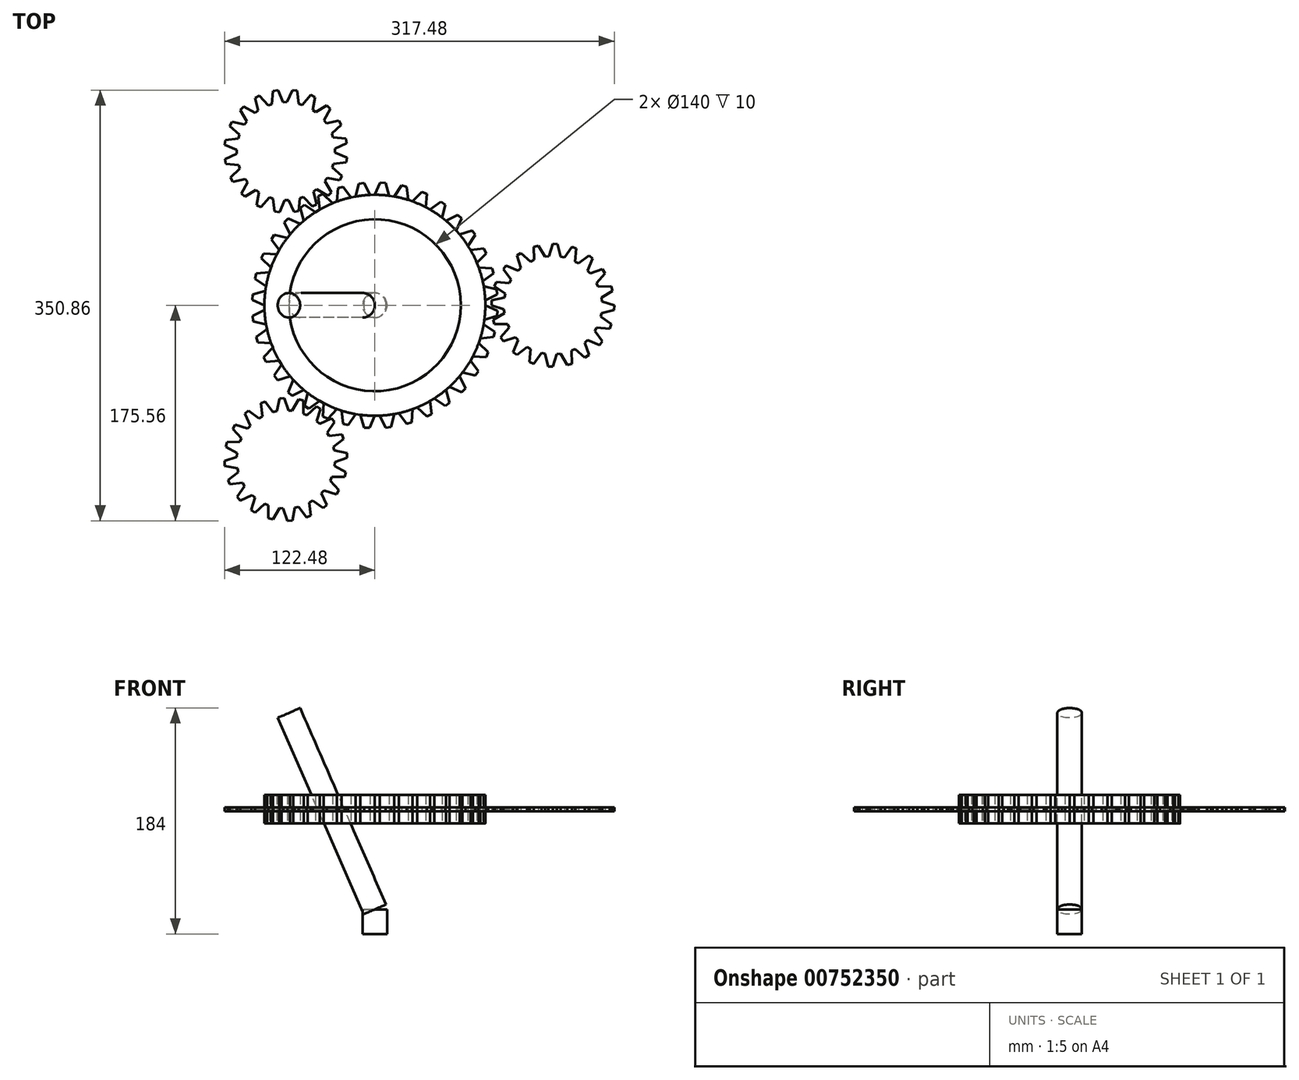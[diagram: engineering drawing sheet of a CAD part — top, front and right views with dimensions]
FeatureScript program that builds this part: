
annotation { "Feature Type Name" : "Feature", "Feature Type Description" : "" }
export const myFeature = defineFeature(function(context is Context, id is Id, definition is map)
    precondition{}
    {
        {
            var Q0;
            Q0=qCreatedBy(makeId("Top.planeOp"),FACE);
            var sketch = newSketch(context, id + "F0", { "sketchPlane" : qUnion([Q0])});
            skLineSegment(sketch, "E0", {"start": v(90, 0) * mm, "end": v(100, 0) * mm});
            skLineSegment(sketch, "E1.4.0", {"start": v(88.63, -15.63) * mm, "end": v(98.48, -17.36) * mm});
            skPoint(sketch, "E1.center", {"position": v(0, 0) * mm});
            skLineSegment(sketch, "E2", {"start": v(90, 0) * mm, "end": v(99.9, -4.36) * mm});
            skLineSegment(sketch, "E3", {"start": v(99.9, -4.36) * mm, "end": v(99.62, -8.72) * mm});
            skLineSegment(sketch, "E4", {"start": v(99.62, -8.72) * mm, "end": v(89.23, -11.75) * mm});
            skLineSegment(sketch, "E5", {"start": v(89.23, -11.75) * mm, "end": v(88.63, -15.63) * mm});
            skLineSegment(sketch, "E6.1.0", {"start": v(88.63, 15.63) * mm, "end": v(99.14, 13.05) * mm});
            skLineSegment(sketch, "E6.1.1", {"start": v(99.14, 13.05) * mm, "end": v(99.62, 8.72) * mm});
            skLineSegment(sketch, "E6.1.2", {"start": v(99.62, 8.72) * mm, "end": v(89.91, 3.93) * mm});
            skLineSegment(sketch, "E6.1.3", {"start": v(89.91, 3.93) * mm, "end": v(90, 0) * mm});
            skLineSegment(sketch, "E6.2.0", {"start": v(84.57, 30.78) * mm, "end": v(95.37, 30.07) * mm});
            skLineSegment(sketch, "E6.2.1", {"start": v(95.37, 30.07) * mm, "end": v(96.6, 25.88) * mm});
            skLineSegment(sketch, "E6.2.2", {"start": v(96.6, 25.88) * mm, "end": v(87.87, 19.48) * mm});
            skLineSegment(sketch, "E6.2.3", {"start": v(87.87, 19.48) * mm, "end": v(88.63, 15.63) * mm});
            skLineSegment(sketch, "E6.3.0", {"start": v(77.94, 45) * mm, "end": v(88.7, 46.17) * mm});
            skLineSegment(sketch, "E6.3.1", {"start": v(88.7, 46.17) * mm, "end": v(90.63, 42.26) * mm});
            skLineSegment(sketch, "E6.3.2", {"start": v(90.63, 42.26) * mm, "end": v(83.15, 34.44) * mm});
            skLineSegment(sketch, "E6.3.3", {"start": v(83.15, 34.44) * mm, "end": v(84.57, 30.78) * mm});
            skLineSegment(sketch, "E6.4.0", {"start": v(68.94, 57.85) * mm, "end": v(79.34, 60.88) * mm});
            skLineSegment(sketch, "E6.4.1", {"start": v(79.34, 60.88) * mm, "end": v(81.92, 57.36) * mm});
            skLineSegment(sketch, "E6.4.2", {"start": v(81.92, 57.36) * mm, "end": v(75.9, 48.36) * mm});
            skLineSegment(sketch, "E6.4.3", {"start": v(75.9, 48.36) * mm, "end": v(77.94, 45) * mm});
            skLineSegment(sketch, "E6.5.0", {"start": v(57.85, 68.94) * mm, "end": v(67.56, 73.73) * mm});
            skLineSegment(sketch, "E6.5.1", {"start": v(67.56, 73.73) * mm, "end": v(70.71, 70.71) * mm});
            skLineSegment(sketch, "E6.5.2", {"start": v(70.71, 70.71) * mm, "end": v(66.35, 60.8) * mm});
            skLineSegment(sketch, "E6.5.3", {"start": v(66.35, 60.8) * mm, "end": v(68.94, 57.85) * mm});
            skLineSegment(sketch, "E6.6.0", {"start": v(45, 77.94) * mm, "end": v(53.73, 84.34) * mm});
            skLineSegment(sketch, "E6.6.1", {"start": v(53.73, 84.34) * mm, "end": v(57.36, 81.92) * mm});
            skLineSegment(sketch, "E6.6.2", {"start": v(57.36, 81.92) * mm, "end": v(54.79, 71.4) * mm});
            skLineSegment(sketch, "E6.6.3", {"start": v(54.79, 71.4) * mm, "end": v(57.85, 68.94) * mm});
            skLineSegment(sketch, "E6.7.0", {"start": v(30.78, 84.57) * mm, "end": v(38.27, 92.39) * mm});
            skLineSegment(sketch, "E6.7.1", {"start": v(38.27, 92.39) * mm, "end": v(42.26, 90.63) * mm});
            skLineSegment(sketch, "E6.7.2", {"start": v(42.26, 90.63) * mm, "end": v(41.56, 79.83) * mm});
            skLineSegment(sketch, "E6.7.3", {"start": v(41.56, 79.83) * mm, "end": v(45, 77.94) * mm});
            skLineSegment(sketch, "E6.8.0", {"start": v(15.63, 88.63) * mm, "end": v(21.64, 97.63) * mm});
            skLineSegment(sketch, "E6.8.1", {"start": v(21.64, 97.63) * mm, "end": v(25.88, 96.6) * mm});
            skLineSegment(sketch, "E6.8.2", {"start": v(25.88, 96.6) * mm, "end": v(27.06, 85.83) * mm});
            skLineSegment(sketch, "E6.8.3", {"start": v(27.06, 85.83) * mm, "end": v(30.78, 84.57) * mm});
            skLineSegment(sketch, "E6.9.0", {"start": v(0, 90) * mm, "end": v(4.36, 99.9) * mm});
            skLineSegment(sketch, "E6.9.1", {"start": v(4.36, 99.9) * mm, "end": v(8.72, 99.62) * mm});
            skLineSegment(sketch, "E6.9.2", {"start": v(8.72, 99.62) * mm, "end": v(11.75, 89.23) * mm});
            skLineSegment(sketch, "E6.9.3", {"start": v(11.75, 89.23) * mm, "end": v(15.63, 88.63) * mm});
            skLineSegment(sketch, "E6.10.0", {"start": v(-15.63, 88.63) * mm, "end": v(-13.05, 99.14) * mm});
            skLineSegment(sketch, "E6.10.1", {"start": v(-13.05, 99.14) * mm, "end": v(-8.72, 99.62) * mm});
            skLineSegment(sketch, "E6.10.2", {"start": v(-8.72, 99.62) * mm, "end": v(-3.93, 89.91) * mm});
            skLineSegment(sketch, "E6.10.3", {"start": v(-3.93, 89.91) * mm, "end": v(0, 90) * mm});
            skLineSegment(sketch, "E6.11.0", {"start": v(-30.78, 84.57) * mm, "end": v(-30.07, 95.37) * mm});
            skLineSegment(sketch, "E6.11.1", {"start": v(-30.07, 95.37) * mm, "end": v(-25.88, 96.6) * mm});
            skLineSegment(sketch, "E6.11.2", {"start": v(-25.88, 96.6) * mm, "end": v(-19.48, 87.87) * mm});
            skLineSegment(sketch, "E6.11.3", {"start": v(-19.48, 87.87) * mm, "end": v(-15.63, 88.63) * mm});
            skLineSegment(sketch, "E6.12.0", {"start": v(-45, 77.94) * mm, "end": v(-46.17, 88.7) * mm});
            skLineSegment(sketch, "E6.12.1", {"start": v(-46.17, 88.7) * mm, "end": v(-42.26, 90.63) * mm});
            skLineSegment(sketch, "E6.12.2", {"start": v(-42.26, 90.63) * mm, "end": v(-34.44, 83.15) * mm});
            skLineSegment(sketch, "E6.12.3", {"start": v(-34.44, 83.15) * mm, "end": v(-30.78, 84.57) * mm});
            skLineSegment(sketch, "E6.13.0", {"start": v(-57.85, 68.94) * mm, "end": v(-60.88, 79.34) * mm});
            skLineSegment(sketch, "E6.13.1", {"start": v(-60.88, 79.34) * mm, "end": v(-57.36, 81.92) * mm});
            skLineSegment(sketch, "E6.13.2", {"start": v(-57.36, 81.92) * mm, "end": v(-48.36, 75.9) * mm});
            skLineSegment(sketch, "E6.13.3", {"start": v(-48.36, 75.9) * mm, "end": v(-45, 77.94) * mm});
            skLineSegment(sketch, "E6.14.0", {"start": v(-68.94, 57.85) * mm, "end": v(-73.73, 67.56) * mm});
            skLineSegment(sketch, "E6.14.1", {"start": v(-73.73, 67.56) * mm, "end": v(-70.71, 70.71) * mm});
            skLineSegment(sketch, "E6.14.2", {"start": v(-70.71, 70.71) * mm, "end": v(-60.8, 66.35) * mm});
            skLineSegment(sketch, "E6.14.3", {"start": v(-60.8, 66.35) * mm, "end": v(-57.85, 68.94) * mm});
            skLineSegment(sketch, "E6.15.0", {"start": v(-77.94, 45) * mm, "end": v(-84.34, 53.73) * mm});
            skLineSegment(sketch, "E6.15.1", {"start": v(-84.34, 53.73) * mm, "end": v(-81.92, 57.36) * mm});
            skLineSegment(sketch, "E6.15.2", {"start": v(-81.92, 57.36) * mm, "end": v(-71.4, 54.79) * mm});
            skLineSegment(sketch, "E6.15.3", {"start": v(-71.4, 54.79) * mm, "end": v(-68.94, 57.85) * mm});
            skLineSegment(sketch, "E6.16.0", {"start": v(-84.57, 30.78) * mm, "end": v(-92.39, 38.27) * mm});
            skLineSegment(sketch, "E6.16.1", {"start": v(-92.39, 38.27) * mm, "end": v(-90.63, 42.26) * mm});
            skLineSegment(sketch, "E6.16.2", {"start": v(-90.63, 42.26) * mm, "end": v(-79.83, 41.56) * mm});
            skLineSegment(sketch, "E6.16.3", {"start": v(-79.83, 41.56) * mm, "end": v(-77.94, 45) * mm});
            skLineSegment(sketch, "E6.17.0", {"start": v(-88.63, 15.63) * mm, "end": v(-97.63, 21.64) * mm});
            skLineSegment(sketch, "E6.17.1", {"start": v(-97.63, 21.64) * mm, "end": v(-96.6, 25.88) * mm});
            skLineSegment(sketch, "E6.17.2", {"start": v(-96.6, 25.88) * mm, "end": v(-85.83, 27.06) * mm});
            skLineSegment(sketch, "E6.17.3", {"start": v(-85.83, 27.06) * mm, "end": v(-84.57, 30.78) * mm});
            skLineSegment(sketch, "E6.18.0", {"start": v(-90, 0) * mm, "end": v(-99.9, 4.36) * mm});
            skLineSegment(sketch, "E6.18.1", {"start": v(-99.9, 4.36) * mm, "end": v(-99.62, 8.72) * mm});
            skLineSegment(sketch, "E6.18.2", {"start": v(-99.62, 8.72) * mm, "end": v(-89.23, 11.75) * mm});
            skLineSegment(sketch, "E6.18.3", {"start": v(-89.23, 11.75) * mm, "end": v(-88.63, 15.63) * mm});
            skLineSegment(sketch, "E6.19.0", {"start": v(-88.63, -15.63) * mm, "end": v(-99.14, -13.05) * mm});
            skLineSegment(sketch, "E6.19.1", {"start": v(-99.14, -13.05) * mm, "end": v(-99.62, -8.72) * mm});
            skLineSegment(sketch, "E6.19.2", {"start": v(-99.62, -8.72) * mm, "end": v(-89.91, -3.93) * mm});
            skLineSegment(sketch, "E6.19.3", {"start": v(-89.91, -3.93) * mm, "end": v(-90, 0) * mm});
            skLineSegment(sketch, "E6.20.0", {"start": v(-84.57, -30.78) * mm, "end": v(-95.37, -30.07) * mm});
            skLineSegment(sketch, "E6.20.1", {"start": v(-95.37, -30.07) * mm, "end": v(-96.6, -25.88) * mm});
            skLineSegment(sketch, "E6.20.2", {"start": v(-96.6, -25.88) * mm, "end": v(-87.87, -19.48) * mm});
            skLineSegment(sketch, "E6.20.3", {"start": v(-87.87, -19.48) * mm, "end": v(-88.63, -15.63) * mm});
            skLineSegment(sketch, "E6.21.0", {"start": v(-77.94, -45) * mm, "end": v(-88.7, -46.17) * mm});
            skLineSegment(sketch, "E6.21.1", {"start": v(-88.7, -46.17) * mm, "end": v(-90.63, -42.26) * mm});
            skLineSegment(sketch, "E6.21.2", {"start": v(-90.63, -42.26) * mm, "end": v(-83.15, -34.44) * mm});
            skLineSegment(sketch, "E6.21.3", {"start": v(-83.15, -34.44) * mm, "end": v(-84.57, -30.78) * mm});
            skLineSegment(sketch, "E6.22.0", {"start": v(-68.94, -57.85) * mm, "end": v(-79.34, -60.88) * mm});
            skLineSegment(sketch, "E6.22.1", {"start": v(-79.34, -60.88) * mm, "end": v(-81.92, -57.36) * mm});
            skLineSegment(sketch, "E6.22.2", {"start": v(-81.92, -57.36) * mm, "end": v(-75.9, -48.36) * mm});
            skLineSegment(sketch, "E6.22.3", {"start": v(-75.9, -48.36) * mm, "end": v(-77.94, -45) * mm});
            skLineSegment(sketch, "E6.23.0", {"start": v(-57.85, -68.94) * mm, "end": v(-67.56, -73.73) * mm});
            skLineSegment(sketch, "E6.23.1", {"start": v(-67.56, -73.73) * mm, "end": v(-70.71, -70.71) * mm});
            skLineSegment(sketch, "E6.23.2", {"start": v(-70.71, -70.71) * mm, "end": v(-66.35, -60.8) * mm});
            skLineSegment(sketch, "E6.23.3", {"start": v(-66.35, -60.8) * mm, "end": v(-68.94, -57.85) * mm});
            skLineSegment(sketch, "E6.24.0", {"start": v(-45, -77.94) * mm, "end": v(-53.73, -84.34) * mm});
            skLineSegment(sketch, "E6.24.1", {"start": v(-53.73, -84.34) * mm, "end": v(-57.36, -81.92) * mm});
            skLineSegment(sketch, "E6.24.2", {"start": v(-57.36, -81.92) * mm, "end": v(-54.79, -71.4) * mm});
            skLineSegment(sketch, "E6.24.3", {"start": v(-54.79, -71.4) * mm, "end": v(-57.85, -68.94) * mm});
            skLineSegment(sketch, "E6.25.0", {"start": v(-30.78, -84.57) * mm, "end": v(-38.27, -92.39) * mm});
            skLineSegment(sketch, "E6.25.1", {"start": v(-38.27, -92.39) * mm, "end": v(-42.26, -90.63) * mm});
            skLineSegment(sketch, "E6.25.2", {"start": v(-42.26, -90.63) * mm, "end": v(-41.56, -79.83) * mm});
            skLineSegment(sketch, "E6.25.3", {"start": v(-41.56, -79.83) * mm, "end": v(-45, -77.94) * mm});
            skLineSegment(sketch, "E6.26.0", {"start": v(-15.63, -88.63) * mm, "end": v(-21.64, -97.63) * mm});
            skLineSegment(sketch, "E6.26.1", {"start": v(-21.64, -97.63) * mm, "end": v(-25.88, -96.6) * mm});
            skLineSegment(sketch, "E6.26.2", {"start": v(-25.88, -96.6) * mm, "end": v(-27.06, -85.83) * mm});
            skLineSegment(sketch, "E6.26.3", {"start": v(-27.06, -85.83) * mm, "end": v(-30.78, -84.57) * mm});
            skLineSegment(sketch, "E6.27.0", {"start": v(0, -90) * mm, "end": v(-4.36, -99.9) * mm});
            skLineSegment(sketch, "E6.27.1", {"start": v(-4.36, -99.9) * mm, "end": v(-8.72, -99.62) * mm});
            skLineSegment(sketch, "E6.27.2", {"start": v(-8.72, -99.62) * mm, "end": v(-11.75, -89.23) * mm});
            skLineSegment(sketch, "E6.27.3", {"start": v(-11.75, -89.23) * mm, "end": v(-15.63, -88.63) * mm});
            skLineSegment(sketch, "E6.28.0", {"start": v(15.63, -88.63) * mm, "end": v(13.05, -99.14) * mm});
            skLineSegment(sketch, "E6.28.1", {"start": v(13.05, -99.14) * mm, "end": v(8.72, -99.62) * mm});
            skLineSegment(sketch, "E6.28.2", {"start": v(8.72, -99.62) * mm, "end": v(3.93, -89.91) * mm});
            skLineSegment(sketch, "E6.28.3", {"start": v(3.93, -89.91) * mm, "end": v(0, -90) * mm});
            skLineSegment(sketch, "E6.29.0", {"start": v(30.78, -84.57) * mm, "end": v(30.07, -95.37) * mm});
            skLineSegment(sketch, "E6.29.1", {"start": v(30.07, -95.37) * mm, "end": v(25.88, -96.6) * mm});
            skLineSegment(sketch, "E6.29.2", {"start": v(25.88, -96.6) * mm, "end": v(19.48, -87.87) * mm});
            skLineSegment(sketch, "E6.29.3", {"start": v(19.48, -87.87) * mm, "end": v(15.63, -88.63) * mm});
            skLineSegment(sketch, "E6.30.0", {"start": v(45, -77.94) * mm, "end": v(46.17, -88.7) * mm});
            skLineSegment(sketch, "E6.30.1", {"start": v(46.17, -88.7) * mm, "end": v(42.26, -90.63) * mm});
            skLineSegment(sketch, "E6.30.2", {"start": v(42.26, -90.63) * mm, "end": v(34.44, -83.15) * mm});
            skLineSegment(sketch, "E6.30.3", {"start": v(34.44, -83.15) * mm, "end": v(30.78, -84.57) * mm});
            skLineSegment(sketch, "E6.31.0", {"start": v(57.85, -68.94) * mm, "end": v(60.88, -79.34) * mm});
            skLineSegment(sketch, "E6.31.1", {"start": v(60.88, -79.34) * mm, "end": v(57.36, -81.92) * mm});
            skLineSegment(sketch, "E6.31.2", {"start": v(57.36, -81.92) * mm, "end": v(48.36, -75.9) * mm});
            skLineSegment(sketch, "E6.31.3", {"start": v(48.36, -75.9) * mm, "end": v(45, -77.94) * mm});
            skLineSegment(sketch, "E6.32.0", {"start": v(68.94, -57.85) * mm, "end": v(73.73, -67.56) * mm});
            skLineSegment(sketch, "E6.32.1", {"start": v(73.73, -67.56) * mm, "end": v(70.71, -70.71) * mm});
            skLineSegment(sketch, "E6.32.2", {"start": v(70.71, -70.71) * mm, "end": v(60.8, -66.35) * mm});
            skLineSegment(sketch, "E6.32.3", {"start": v(60.8, -66.35) * mm, "end": v(57.85, -68.94) * mm});
            skLineSegment(sketch, "E6.33.0", {"start": v(77.94, -45) * mm, "end": v(84.34, -53.73) * mm});
            skLineSegment(sketch, "E6.33.1", {"start": v(84.34, -53.73) * mm, "end": v(81.92, -57.36) * mm});
            skLineSegment(sketch, "E6.33.2", {"start": v(81.92, -57.36) * mm, "end": v(71.4, -54.79) * mm});
            skLineSegment(sketch, "E6.33.3", {"start": v(71.4, -54.79) * mm, "end": v(68.94, -57.85) * mm});
            skLineSegment(sketch, "E6.34.0", {"start": v(84.57, -30.78) * mm, "end": v(92.39, -38.27) * mm});
            skLineSegment(sketch, "E6.34.1", {"start": v(92.39, -38.27) * mm, "end": v(90.63, -42.26) * mm});
            skLineSegment(sketch, "E6.34.2", {"start": v(90.63, -42.26) * mm, "end": v(79.83, -41.56) * mm});
            skLineSegment(sketch, "E6.34.3", {"start": v(79.83, -41.56) * mm, "end": v(77.94, -45) * mm});
            skLineSegment(sketch, "E6.35.0", {"start": v(88.63, -15.63) * mm, "end": v(97.63, -21.64) * mm});
            skLineSegment(sketch, "E6.35.1", {"start": v(97.63, -21.64) * mm, "end": v(96.6, -25.88) * mm});
            skLineSegment(sketch, "E6.35.2", {"start": v(96.6, -25.88) * mm, "end": v(85.83, -27.06) * mm});
            skLineSegment(sketch, "E6.35.3", {"start": v(85.83, -27.06) * mm, "end": v(84.57, -30.78) * mm});
            skLineSegment(sketch, "E7", {"start": v(145, 0) * mm, "end": v(90, 0) * mm});
            skPoint(sketch, "E8.center", {"position": v(145, 0) * mm});
            skLineSegment(sketch, "E8.anchor1", {"start": v(145, 0) * mm, "end": v(90, 0) * mm, "construction": true});
            skLineSegment(sketch, "E9", {"start": v(95.15, 3.92) * mm, "end": v(105.5, 6.26) * mm});
            skLineSegment(sketch, "E10", {"start": v(95.15, 3.92) * mm, "end": v(95, 0) * mm});
            skLineSegment(sketch, "E11", {"start": v(105.5, 6.26) * mm, "end": v(106.1, 9.34) * mm});
            skLineSegment(sketch, "E12", {"start": v(106.1, 9.34) * mm, "end": v(97.45, 15.45) * mm});
            skLineSegment(sketch, "E13.1.0", {"start": v(96.38, -11.67) * mm, "end": v(97.45, -15.45) * mm});
            skLineSegment(sketch, "E13.1.1", {"start": v(96.38, -11.67) * mm, "end": v(105.5, -6.26) * mm});
            skLineSegment(sketch, "E13.1.2", {"start": v(105.5, -6.26) * mm, "end": v(105.12, -3.14) * mm});
            skLineSegment(sketch, "E13.1.3", {"start": v(105.12, -3.14) * mm, "end": v(95, 0) * mm});
            skLineSegment(sketch, "E13.2.0", {"start": v(102.37, -26.12) * mm, "end": v(104.55, -29.39) * mm});
            skLineSegment(sketch, "E13.2.1", {"start": v(102.37, -26.12) * mm, "end": v(109.36, -18.16) * mm});
            skLineSegment(sketch, "E13.2.2", {"start": v(109.36, -18.16) * mm, "end": v(108.04, -15.3) * mm});
            skLineSegment(sketch, "E13.2.3", {"start": v(108.04, -15.3) * mm, "end": v(97.45, -15.45) * mm});
            skLineSegment(sketch, "E13.3.0", {"start": v(112.53, -38.02) * mm, "end": v(115.61, -40.45) * mm});
            skLineSegment(sketch, "E13.3.1", {"start": v(112.53, -38.02) * mm, "end": v(116.72, -28.28) * mm});
            skLineSegment(sketch, "E13.3.2", {"start": v(116.72, -28.28) * mm, "end": v(114.58, -25.98) * mm});
            skLineSegment(sketch, "E13.3.3", {"start": v(114.58, -25.98) * mm, "end": v(104.55, -29.39) * mm});
            skLineSegment(sketch, "E13.4.0", {"start": v(125.87, -46.2) * mm, "end": v(129.55, -47.55) * mm});
            skLineSegment(sketch, "E13.4.1", {"start": v(125.87, -46.2) * mm, "end": v(126.84, -35.64) * mm});
            skLineSegment(sketch, "E13.4.2", {"start": v(126.84, -35.64) * mm, "end": v(124.1, -34.1) * mm});
            skLineSegment(sketch, "E13.4.3", {"start": v(124.1, -34.1) * mm, "end": v(115.61, -40.45) * mm});
            skLineSegment(sketch, "E13.5.0", {"start": v(141.08, -49.85) * mm, "end": v(145, -50) * mm});
            skLineSegment(sketch, "E13.5.1", {"start": v(141.08, -49.85) * mm, "end": v(138.74, -39.5) * mm});
            skLineSegment(sketch, "E13.5.2", {"start": v(138.74, -39.5) * mm, "end": v(135.66, -38.9) * mm});
            skLineSegment(sketch, "E13.5.3", {"start": v(135.66, -38.9) * mm, "end": v(129.55, -47.55) * mm});
            skLineSegment(sketch, "E13.6.0", {"start": v(156.67, -48.62) * mm, "end": v(160.45, -47.55) * mm});
            skLineSegment(sketch, "E13.6.1", {"start": v(156.67, -48.62) * mm, "end": v(151.26, -39.5) * mm});
            skLineSegment(sketch, "E13.6.2", {"start": v(151.26, -39.5) * mm, "end": v(148.14, -39.88) * mm});
            skLineSegment(sketch, "E13.6.3", {"start": v(148.14, -39.88) * mm, "end": v(145, -50) * mm});
            skLineSegment(sketch, "E13.7.0", {"start": v(171.12, -42.63) * mm, "end": v(174.39, -40.45) * mm});
            skLineSegment(sketch, "E13.7.1", {"start": v(171.12, -42.63) * mm, "end": v(163.16, -35.64) * mm});
            skLineSegment(sketch, "E13.7.2", {"start": v(163.16, -35.64) * mm, "end": v(160.3, -36.96) * mm});
            skLineSegment(sketch, "E13.7.3", {"start": v(160.3, -36.96) * mm, "end": v(160.45, -47.55) * mm});
            skLineSegment(sketch, "E13.8.0", {"start": v(183.02, -32.47) * mm, "end": v(185.45, -29.39) * mm});
            skLineSegment(sketch, "E13.8.1", {"start": v(183.02, -32.47) * mm, "end": v(173.28, -28.28) * mm});
            skLineSegment(sketch, "E13.8.2", {"start": v(173.28, -28.28) * mm, "end": v(170.98, -30.42) * mm});
            skLineSegment(sketch, "E13.8.3", {"start": v(170.98, -30.42) * mm, "end": v(174.39, -40.45) * mm});
            skLineSegment(sketch, "E13.9.0", {"start": v(191.2, -19.13) * mm, "end": v(192.55, -15.45) * mm});
            skLineSegment(sketch, "E13.9.1", {"start": v(191.2, -19.13) * mm, "end": v(180.64, -18.16) * mm});
            skLineSegment(sketch, "E13.9.2", {"start": v(180.64, -18.16) * mm, "end": v(179.1, -20.9) * mm});
            skLineSegment(sketch, "E13.9.3", {"start": v(179.1, -20.9) * mm, "end": v(185.45, -29.39) * mm});
            skLineSegment(sketch, "E13.10.0", {"start": v(194.85, -3.92) * mm, "end": v(195, 0) * mm});
            skLineSegment(sketch, "E13.10.1", {"start": v(194.85, -3.92) * mm, "end": v(184.5, -6.26) * mm});
            skLineSegment(sketch, "E13.10.2", {"start": v(184.5, -6.26) * mm, "end": v(183.9, -9.34) * mm});
            skLineSegment(sketch, "E13.10.3", {"start": v(183.9, -9.34) * mm, "end": v(192.55, -15.45) * mm});
            skLineSegment(sketch, "E13.11.0", {"start": v(193.62, 11.67) * mm, "end": v(192.55, 15.45) * mm});
            skLineSegment(sketch, "E13.11.1", {"start": v(193.62, 11.67) * mm, "end": v(184.5, 6.26) * mm});
            skLineSegment(sketch, "E13.11.2", {"start": v(184.5, 6.26) * mm, "end": v(184.88, 3.14) * mm});
            skLineSegment(sketch, "E13.11.3", {"start": v(184.88, 3.14) * mm, "end": v(195, 0) * mm});
            skLineSegment(sketch, "E13.12.0", {"start": v(187.63, 26.12) * mm, "end": v(185.45, 29.39) * mm});
            skLineSegment(sketch, "E13.12.1", {"start": v(187.63, 26.12) * mm, "end": v(180.64, 18.16) * mm});
            skLineSegment(sketch, "E13.12.2", {"start": v(180.64, 18.16) * mm, "end": v(181.96, 15.3) * mm});
            skLineSegment(sketch, "E13.12.3", {"start": v(181.96, 15.3) * mm, "end": v(192.55, 15.45) * mm});
            skLineSegment(sketch, "E13.13.0", {"start": v(177.47, 38.02) * mm, "end": v(174.39, 40.45) * mm});
            skLineSegment(sketch, "E13.13.1", {"start": v(177.47, 38.02) * mm, "end": v(173.28, 28.28) * mm});
            skLineSegment(sketch, "E13.13.2", {"start": v(173.28, 28.28) * mm, "end": v(175.42, 25.98) * mm});
            skLineSegment(sketch, "E13.13.3", {"start": v(175.42, 25.98) * mm, "end": v(185.45, 29.39) * mm});
            skLineSegment(sketch, "E13.14.0", {"start": v(164.13, 46.2) * mm, "end": v(160.45, 47.55) * mm});
            skLineSegment(sketch, "E13.14.1", {"start": v(164.13, 46.2) * mm, "end": v(163.16, 35.64) * mm});
            skLineSegment(sketch, "E13.14.2", {"start": v(163.16, 35.64) * mm, "end": v(165.9, 34.1) * mm});
            skLineSegment(sketch, "E13.14.3", {"start": v(165.9, 34.1) * mm, "end": v(174.39, 40.45) * mm});
            skLineSegment(sketch, "E13.15.0", {"start": v(148.92, 49.85) * mm, "end": v(145, 50) * mm});
            skLineSegment(sketch, "E13.15.1", {"start": v(148.92, 49.85) * mm, "end": v(151.26, 39.5) * mm});
            skLineSegment(sketch, "E13.15.2", {"start": v(151.26, 39.5) * mm, "end": v(154.34, 38.9) * mm});
            skLineSegment(sketch, "E13.15.3", {"start": v(154.34, 38.9) * mm, "end": v(160.45, 47.55) * mm});
            skLineSegment(sketch, "E13.16.0", {"start": v(133.33, 48.62) * mm, "end": v(129.55, 47.55) * mm});
            skLineSegment(sketch, "E13.16.1", {"start": v(133.33, 48.62) * mm, "end": v(138.74, 39.5) * mm});
            skLineSegment(sketch, "E13.16.2", {"start": v(138.74, 39.5) * mm, "end": v(141.86, 39.88) * mm});
            skLineSegment(sketch, "E13.16.3", {"start": v(141.86, 39.88) * mm, "end": v(145, 50) * mm});
            skLineSegment(sketch, "E13.17.0", {"start": v(118.88, 42.63) * mm, "end": v(115.61, 40.45) * mm});
            skLineSegment(sketch, "E13.17.1", {"start": v(118.88, 42.63) * mm, "end": v(126.84, 35.64) * mm});
            skLineSegment(sketch, "E13.17.2", {"start": v(126.84, 35.64) * mm, "end": v(129.7, 36.96) * mm});
            skLineSegment(sketch, "E13.17.3", {"start": v(129.7, 36.96) * mm, "end": v(129.55, 47.55) * mm});
            skLineSegment(sketch, "E13.18.0", {"start": v(106.98, 32.47) * mm, "end": v(104.55, 29.39) * mm});
            skLineSegment(sketch, "E13.18.1", {"start": v(106.98, 32.47) * mm, "end": v(116.72, 28.28) * mm});
            skLineSegment(sketch, "E13.18.2", {"start": v(116.72, 28.28) * mm, "end": v(119.02, 30.42) * mm});
            skLineSegment(sketch, "E13.18.3", {"start": v(119.02, 30.42) * mm, "end": v(115.61, 40.45) * mm});
            skLineSegment(sketch, "E13.19.0", {"start": v(98.8, 19.13) * mm, "end": v(97.45, 15.45) * mm});
            skLineSegment(sketch, "E13.19.1", {"start": v(98.8, 19.13) * mm, "end": v(109.36, 18.16) * mm});
            skLineSegment(sketch, "E13.19.2", {"start": v(109.36, 18.16) * mm, "end": v(110.9, 20.9) * mm});
            skLineSegment(sketch, "E13.19.3", {"start": v(110.9, 20.9) * mm, "end": v(104.55, 29.39) * mm});
            skLineSegment(sketch, "E14.1.0", {"start": v(-104.23, 149.92) * mm, "end": v(-109.66, 159.03) * mm});
            skLineSegment(sketch, "E14.1.1", {"start": v(-73.55, 85.59) * mm, "end": v(-77.73, 75.85) * mm});
            skLineSegment(sketch, "E14.1.2", {"start": v(-34.8, 112.22) * mm, "end": v(-26.82, 105.24) * mm});
            skPoint(sketch, "E14.1.3", {"position": v(-72.5, 125.57) * mm});
            skPoint(sketch, "E14.1.4", {"position": v(-72.5, 125.57) * mm});
            skLineSegment(sketch, "E14.1.5", {"start": v(-83.86, 163.93) * mm, "end": v(-82.9, 174.48) * mm});
            skLineSegment(sketch, "E14.1.6", {"start": v(-27.37, 147.1) * mm, "end": v(-35.16, 139.9) * mm});
            skLineSegment(sketch, "E14.1.7", {"start": v(-96.36, 81.63) * mm, "end": v(-94.29, 92.03) * mm});
            skLineSegment(sketch, "E14.1.8", {"start": v(-121.66, 134.69) * mm, "end": v(-111.14, 135.93) * mm});
            skLineSegment(sketch, "E14.1.9", {"start": v(-112.49, 126.62) * mm, "end": v(-122.23, 130.8) * mm});
            skLineSegment(sketch, "E14.1.10", {"start": v(-79.03, 175.15) * mm, "end": v(-74.6, 165.52) * mm});
            skLineSegment(sketch, "E14.1.11", {"start": v(-33.86, 115.22) * mm, "end": v(-34.8, 112.22) * mm});
            skLineSegment(sketch, "E14.1.12", {"start": v(-50.71, 159.12) * mm, "end": v(-48.15, 157.3) * mm});
            skLineSegment(sketch, "E14.1.13", {"start": v(-97.67, 156.66) * mm, "end": v(-95.16, 158.54) * mm});
            skLineSegment(sketch, "E14.1.14", {"start": v(-109.84, 111.24) * mm, "end": v(-110.85, 114.21) * mm});
            skLineSegment(sketch, "E14.1.15", {"start": v(-32.55, 127.67) * mm, "end": v(-32.51, 124.53) * mm});
            skLineSegment(sketch, "E14.1.16", {"start": v(-62.15, 164.21) * mm, "end": v(-59.15, 163.28) * mm});
            skLineSegment(sketch, "E14.1.17", {"start": v(-106.05, 147.36) * mm, "end": v(-104.23, 149.92) * mm});
            skLineSegment(sketch, "E14.1.18", {"start": v(-103.59, 100.4) * mm, "end": v(-105.47, 102.92) * mm});
            skLineSegment(sketch, "E14.1.19", {"start": v(-58.17, 88.23) * mm, "end": v(-61.14, 87.22) * mm});
            skLineSegment(sketch, "E14.1.20", {"start": v(-63.39, 174.74) * mm, "end": v(-62.15, 164.21) * mm});
            skLineSegment(sketch, "E14.1.21", {"start": v(-22.93, 132.1) * mm, "end": v(-32.55, 127.67) * mm});
            skLineSegment(sketch, "E14.1.22", {"start": v(-108.77, 91.16) * mm, "end": v(-103.59, 100.4) * mm});
            skLineSegment(sketch, "E14.1.23", {"start": v(-116.44, 149.43) * mm, "end": v(-106.05, 147.36) * mm});
            skLineSegment(sketch, "E14.1.24", {"start": v(-22.93, 132.1) * mm, "end": v(-23.6, 135.97) * mm});
            skLineSegment(sketch, "E14.1.25", {"start": v(-63.39, 174.74) * mm, "end": v(-67.27, 175.3) * mm});
            skLineSegment(sketch, "E14.1.26", {"start": v(-116.44, 149.43) * mm, "end": v(-118.18, 145.91) * mm});
            skLineSegment(sketch, "E14.1.27", {"start": v(-108.77, 91.16) * mm, "end": v(-105.96, 88.42) * mm});
            skLineSegment(sketch, "E14.1.28", {"start": v(-105.47, 102.92) * mm, "end": v(-115.8, 100.57) * mm});
            skLineSegment(sketch, "E14.1.29", {"start": v(-82.85, 86.94) * mm, "end": v(-85.85, 87.87) * mm});
            skLineSegment(sketch, "E14.1.30", {"start": v(-41.41, 150.75) * mm, "end": v(-39.53, 148.23) * mm});
            skLineSegment(sketch, "E14.1.31", {"start": v(-38.95, 103.79) * mm, "end": v(-40.77, 101.22) * mm});
            skLineSegment(sketch, "E14.1.32", {"start": v(-48.15, 157.3) * mm, "end": v(-39.04, 162.73) * mm});
            skLineSegment(sketch, "E14.1.33", {"start": v(-95.16, 158.54) * mm, "end": v(-97.5, 168.87) * mm});
            skLineSegment(sketch, "E14.1.34", {"start": v(-86.83, 162.92) * mm, "end": v(-83.86, 163.93) * mm});
            skLineSegment(sketch, "E14.1.35", {"start": v(-110.85, 114.21) * mm, "end": v(-121.4, 115.18) * mm});
            skLineSegment(sketch, "E14.1.36", {"start": v(-70.4, 85.63) * mm, "end": v(-73.55, 85.59) * mm});
            skLineSegment(sketch, "E14.1.37", {"start": v(-111.14, 135.93) * mm, "end": v(-110.2, 138.93) * mm});
            skLineSegment(sketch, "E14.1.38", {"start": v(-59.15, 163.28) * mm, "end": v(-52.16, 171.25) * mm});
            skLineSegment(sketch, "E14.1.39", {"start": v(-94.29, 92.03) * mm, "end": v(-96.85, 93.84) * mm});
            skLineSegment(sketch, "E14.1.40", {"start": v(-47.33, 94.49) * mm, "end": v(-49.84, 92.6) * mm});
            skLineSegment(sketch, "E14.1.41", {"start": v(-27.37, 147.1) * mm, "end": v(-29.2, 150.57) * mm});
            skLineSegment(sketch, "E14.1.42", {"start": v(-110.2, 138.93) * mm, "end": v(-118.18, 145.91) * mm});
            skLineSegment(sketch, "E14.1.43", {"start": v(-96.85, 93.84) * mm, "end": v(-105.96, 88.42) * mm});
            skLineSegment(sketch, "E14.1.44", {"start": v(-34.15, 136.93) * mm, "end": v(-23.6, 135.97) * mm});
            skLineSegment(sketch, "E14.1.45", {"start": v(-71.45, 165.56) * mm, "end": v(-67.27, 175.3) * mm});
            skLineSegment(sketch, "E14.1.46", {"start": v(-32.51, 124.53) * mm, "end": v(-22.77, 120.35) * mm});
            skLineSegment(sketch, "E14.1.47", {"start": v(-35.16, 139.9) * mm, "end": v(-34.15, 136.93) * mm});
            skLineSegment(sketch, "E14.1.48", {"start": v(-74.6, 165.52) * mm, "end": v(-71.45, 165.56) * mm});
            skLineSegment(sketch, "E14.1.49", {"start": v(-39.53, 148.23) * mm, "end": v(-29.2, 150.57) * mm});
            skLineSegment(sketch, "E14.1.50", {"start": v(-85.85, 87.87) * mm, "end": v(-92.84, 79.9) * mm});
            skLineSegment(sketch, "E14.1.51", {"start": v(-121.66, 134.69) * mm, "end": v(-122.23, 130.8) * mm});
            skLineSegment(sketch, "E14.1.52", {"start": v(-117.63, 104.05) * mm, "end": v(-115.8, 100.57) * mm});
            skLineSegment(sketch, "E14.1.53", {"start": v(-106.92, 161.84) * mm, "end": v(-109.66, 159.03) * mm});
            skLineSegment(sketch, "E14.1.54", {"start": v(-48.64, 169.51) * mm, "end": v(-52.16, 171.25) * mm});
            skLineSegment(sketch, "E14.1.55", {"start": v(-79.03, 175.15) * mm, "end": v(-82.9, 174.48) * mm});
            skLineSegment(sketch, "E14.1.56", {"start": v(-122.07, 119.05) * mm, "end": v(-112.45, 123.48) * mm});
            skLineSegment(sketch, "E14.1.57", {"start": v(-23.34, 116.46) * mm, "end": v(-22.77, 120.35) * mm});
            skLineSegment(sketch, "E14.1.58", {"start": v(-96.36, 81.63) * mm, "end": v(-92.84, 79.9) * mm});
            skLineSegment(sketch, "E14.1.59", {"start": v(-94.03, 170.7) * mm, "end": v(-86.83, 162.92) * mm});
            skLineSegment(sketch, "E14.1.60", {"start": v(-36.23, 160) * mm, "end": v(-41.41, 150.75) * mm});
            skLineSegment(sketch, "E14.1.61", {"start": v(-36.23, 160) * mm, "end": v(-39.04, 162.73) * mm});
            skLineSegment(sketch, "E14.1.62", {"start": v(-23.34, 116.46) * mm, "end": v(-33.86, 115.22) * mm});
            skLineSegment(sketch, "E14.1.63", {"start": v(-122.07, 119.05) * mm, "end": v(-121.4, 115.18) * mm});
            skLineSegment(sketch, "E14.1.64", {"start": v(-81.61, 76.41) * mm, "end": v(-77.73, 75.85) * mm});
            skLineSegment(sketch, "E14.1.65", {"start": v(-112.45, 123.48) * mm, "end": v(-112.49, 126.62) * mm});
            skLineSegment(sketch, "E14.1.66", {"start": v(-94.03, 170.7) * mm, "end": v(-97.5, 168.87) * mm});
            skLineSegment(sketch, "E14.1.67", {"start": v(-106.92, 161.84) * mm, "end": v(-97.67, 156.66) * mm});
            skLineSegment(sketch, "E14.1.68", {"start": v(-81.61, 76.41) * mm, "end": v(-82.85, 86.94) * mm});
            skLineSegment(sketch, "E14.1.69", {"start": v(-117.63, 104.05) * mm, "end": v(-109.84, 111.24) * mm});
            skLineSegment(sketch, "E14.1.70", {"start": v(-48.64, 169.51) * mm, "end": v(-50.71, 159.12) * mm});
            skLineSegment(sketch, "E14.1.71", {"start": v(-65.97, 76) * mm, "end": v(-70.4, 85.63) * mm});
            skLineSegment(sketch, "E14.1.72", {"start": v(-65.97, 76) * mm, "end": v(-62.1, 76.67) * mm});
            skLineSegment(sketch, "E14.1.73", {"start": v(-61.14, 87.22) * mm, "end": v(-62.1, 76.67) * mm});
            skLineSegment(sketch, "E14.1.74", {"start": v(-50.97, 80.44) * mm, "end": v(-58.17, 88.23) * mm});
            skLineSegment(sketch, "E14.1.75", {"start": v(-50.97, 80.44) * mm, "end": v(-47.5, 82.27) * mm});
            skLineSegment(sketch, "E14.1.76", {"start": v(-49.84, 92.6) * mm, "end": v(-47.5, 82.27) * mm});
            skLineSegment(sketch, "E14.1.77", {"start": v(-38.08, 89.3) * mm, "end": v(-47.33, 94.49) * mm});
            skLineSegment(sketch, "E14.1.78", {"start": v(-38.08, 89.3) * mm, "end": v(-35.34, 92.12) * mm});
            skLineSegment(sketch, "E14.1.79", {"start": v(-40.77, 101.22) * mm, "end": v(-35.34, 92.12) * mm});
            skLineSegment(sketch, "E14.1.80", {"start": v(-28.56, 101.72) * mm, "end": v(-38.95, 103.79) * mm});
            skLineSegment(sketch, "E14.1.81", {"start": v(-28.56, 101.72) * mm, "end": v(-26.82, 105.24) * mm});
            skLineSegment(sketch, "E14.2.0", {"start": v(-77.72, -165.23) * mm, "end": v(-82.9, -174.48) * mm});
            skLineSegment(sketch, "E14.2.1", {"start": v(-37.35, -106.49) * mm, "end": v(-26.82, -105.24) * mm});
            skLineSegment(sketch, "E14.2.2", {"start": v(-79.79, -86.24) * mm, "end": v(-77.73, -75.85) * mm});
            skPoint(sketch, "E14.2.3", {"position": v(-72.5, -125.57) * mm});
            skPoint(sketch, "E14.2.4", {"position": v(-72.5, -125.57) * mm});
            skLineSegment(sketch, "E14.2.5", {"start": v(-100.03, -154.59) * mm, "end": v(-109.66, -159.03) * mm});
            skLineSegment(sketch, "E14.2.6", {"start": v(-113.7, -97.25) * mm, "end": v(-103.59, -100.4) * mm});
            skLineSegment(sketch, "E14.2.7", {"start": v(-22.52, -124.26) * mm, "end": v(-32.55, -127.67) * mm});
            skLineSegment(sketch, "E14.2.8", {"start": v(-55.8, -172.7) * mm, "end": v(-62.15, -164.21) * mm});
            skLineSegment(sketch, "E14.2.9", {"start": v(-53.41, -160.73) * mm, "end": v(-52.16, -171.25) * mm});
            skLineSegment(sketch, "E14.2.10", {"start": v(-112.17, -156.01) * mm, "end": v(-106.05, -147.36) * mm});
            skLineSegment(sketch, "E14.2.11", {"start": v(-82.85, -86.94) * mm, "end": v(-79.79, -86.24) * mm});
            skLineSegment(sketch, "E14.2.12", {"start": v(-112.45, -123.48) * mm, "end": v(-112.16, -120.35) * mm});
            skLineSegment(sketch, "E14.2.13", {"start": v(-86.83, -162.92) * mm, "end": v(-89.72, -161.68) * mm});
            skLineSegment(sketch, "E14.2.14", {"start": v(-41.41, -150.75) * mm, "end": v(-43.49, -153.1) * mm});
            skLineSegment(sketch, "E14.2.15", {"start": v(-94.29, -92.03) * mm, "end": v(-91.59, -90.42) * mm});
            skLineSegment(sketch, "E14.2.16", {"start": v(-111.14, -135.93) * mm, "end": v(-111.83, -132.86) * mm});
            skLineSegment(sketch, "E14.2.17", {"start": v(-74.6, -165.52) * mm, "end": v(-77.72, -165.23) * mm});
            skLineSegment(sketch, "E14.2.18", {"start": v(-35.16, -139.9) * mm, "end": v(-36.4, -142.8) * mm});
            skLineSegment(sketch, "E14.2.19", {"start": v(-47.33, -94.49) * mm, "end": v(-44.97, -96.56) * mm});
            skLineSegment(sketch, "E14.2.20", {"start": v(-119.63, -142.26) * mm, "end": v(-111.14, -135.93) * mm});
            skLineSegment(sketch, "E14.2.21", {"start": v(-102.94, -85.9) * mm, "end": v(-94.29, -92.03) * mm});
            skLineSegment(sketch, "E14.2.22", {"start": v(-24.56, -139.77) * mm, "end": v(-35.16, -139.9) * mm});
            skLineSegment(sketch, "E14.2.23", {"start": v(-71.2, -175.56) * mm, "end": v(-74.6, -165.52) * mm});
            skLineSegment(sketch, "E14.2.24", {"start": v(-102.94, -85.9) * mm, "end": v(-105.96, -88.42) * mm});
            skLineSegment(sketch, "E14.2.25", {"start": v(-119.63, -142.26) * mm, "end": v(-118.18, -145.91) * mm});
            skLineSegment(sketch, "E14.2.26", {"start": v(-71.2, -175.56) * mm, "end": v(-67.27, -175.3) * mm});
            skLineSegment(sketch, "E14.2.27", {"start": v(-24.56, -139.77) * mm, "end": v(-23.6, -135.97) * mm});
            skLineSegment(sketch, "E14.2.28", {"start": v(-36.4, -142.8) * mm, "end": v(-29.2, -150.57) * mm});
            skLineSegment(sketch, "E14.2.29", {"start": v(-33.86, -115.22) * mm, "end": v(-33.17, -118.28) * mm});
            skLineSegment(sketch, "E14.2.30", {"start": v(-109.84, -111.24) * mm, "end": v(-108.6, -108.35) * mm});
            skLineSegment(sketch, "E14.2.31", {"start": v(-70.4, -85.63) * mm, "end": v(-67.28, -85.92) * mm});
            skLineSegment(sketch, "E14.2.32", {"start": v(-112.16, -120.35) * mm, "end": v(-121.4, -115.18) * mm});
            skLineSegment(sketch, "E14.2.33", {"start": v(-89.72, -161.68) * mm, "end": v(-97.5, -168.87) * mm});
            skLineSegment(sketch, "E14.2.34", {"start": v(-97.67, -156.66) * mm, "end": v(-100.03, -154.59) * mm});
            skLineSegment(sketch, "E14.2.35", {"start": v(-43.49, -153.1) * mm, "end": v(-39.04, -162.73) * mm});
            skLineSegment(sketch, "E14.2.36", {"start": v(-38.95, -103.79) * mm, "end": v(-37.35, -106.49) * mm});
            skLineSegment(sketch, "E14.2.37", {"start": v(-62.15, -164.21) * mm, "end": v(-65.21, -164.9) * mm});
            skLineSegment(sketch, "E14.2.38", {"start": v(-111.83, -132.86) * mm, "end": v(-122.23, -130.8) * mm});
            skLineSegment(sketch, "E14.2.39", {"start": v(-32.55, -127.67) * mm, "end": v(-32.84, -130.8) * mm});
            skLineSegment(sketch, "E14.2.40", {"start": v(-58.17, -88.23) * mm, "end": v(-55.28, -89.47) * mm});
            skLineSegment(sketch, "E14.2.41", {"start": v(-113.7, -97.25) * mm, "end": v(-115.8, -100.57) * mm});
            skLineSegment(sketch, "E14.2.42", {"start": v(-65.21, -164.9) * mm, "end": v(-67.27, -175.3) * mm});
            skLineSegment(sketch, "E14.2.43", {"start": v(-32.84, -130.8) * mm, "end": v(-23.6, -135.97) * mm});
            skLineSegment(sketch, "E14.2.44", {"start": v(-101.51, -98.04) * mm, "end": v(-105.96, -88.42) * mm});
            skLineSegment(sketch, "E14.2.45", {"start": v(-107.65, -144.66) * mm, "end": v(-118.18, -145.91) * mm});
            skLineSegment(sketch, "E14.2.46", {"start": v(-91.59, -90.42) * mm, "end": v(-92.84, -79.9) * mm});
            skLineSegment(sketch, "E14.2.47", {"start": v(-103.59, -100.4) * mm, "end": v(-101.51, -98.04) * mm});
            skLineSegment(sketch, "E14.2.48", {"start": v(-106.05, -147.36) * mm, "end": v(-107.65, -144.66) * mm});
            skLineSegment(sketch, "E14.2.49", {"start": v(-108.6, -108.35) * mm, "end": v(-115.8, -100.57) * mm});
            skLineSegment(sketch, "E14.2.50", {"start": v(-33.17, -118.28) * mm, "end": v(-22.77, -120.35) * mm});
            skLineSegment(sketch, "E14.2.51", {"start": v(-55.8, -172.7) * mm, "end": v(-52.16, -171.25) * mm});
            skLineSegment(sketch, "E14.2.52", {"start": v(-31.3, -153.9) * mm, "end": v(-29.2, -150.57) * mm});
            skLineSegment(sketch, "E14.2.53", {"start": v(-86.7, -173.51) * mm, "end": v(-82.9, -174.48) * mm});
            skLineSegment(sketch, "E14.2.54", {"start": v(-122.48, -126.88) * mm, "end": v(-122.23, -130.8) * mm});
            skLineSegment(sketch, "E14.2.55", {"start": v(-112.17, -156.01) * mm, "end": v(-109.66, -159.03) * mm});
            skLineSegment(sketch, "E14.2.56", {"start": v(-42.06, -165.24) * mm, "end": v(-50.71, -159.12) * mm});
            skLineSegment(sketch, "E14.2.57", {"start": v(-89.2, -78.44) * mm, "end": v(-92.84, -79.9) * mm});
            skLineSegment(sketch, "E14.2.58", {"start": v(-22.52, -124.26) * mm, "end": v(-22.77, -120.35) * mm});
            skLineSegment(sketch, "E14.2.59", {"start": v(-100.82, -166.78) * mm, "end": v(-97.67, -156.66) * mm});
            skLineSegment(sketch, "E14.2.60", {"start": v(-120.44, -111.37) * mm, "end": v(-109.84, -111.24) * mm});
            skLineSegment(sketch, "E14.2.61", {"start": v(-120.44, -111.37) * mm, "end": v(-121.4, -115.18) * mm});
            skLineSegment(sketch, "E14.2.62", {"start": v(-89.2, -78.44) * mm, "end": v(-82.85, -86.94) * mm});
            skLineSegment(sketch, "E14.2.63", {"start": v(-42.06, -165.24) * mm, "end": v(-39.04, -162.73) * mm});
            skLineSegment(sketch, "E14.2.64", {"start": v(-25.37, -108.88) * mm, "end": v(-26.82, -105.24) * mm});
            skLineSegment(sketch, "E14.2.65", {"start": v(-50.71, -159.12) * mm, "end": v(-53.41, -160.73) * mm});
            skLineSegment(sketch, "E14.2.66", {"start": v(-100.82, -166.78) * mm, "end": v(-97.5, -168.87) * mm});
            skLineSegment(sketch, "E14.2.67", {"start": v(-86.7, -173.51) * mm, "end": v(-86.83, -162.92) * mm});
            skLineSegment(sketch, "E14.2.68", {"start": v(-25.37, -108.88) * mm, "end": v(-33.86, -115.22) * mm});
            skLineSegment(sketch, "E14.2.69", {"start": v(-31.3, -153.9) * mm, "end": v(-41.41, -150.75) * mm});
            skLineSegment(sketch, "E14.2.70", {"start": v(-122.48, -126.88) * mm, "end": v(-112.45, -123.48) * mm});
            skLineSegment(sketch, "E14.2.71", {"start": v(-32.83, -95.14) * mm, "end": v(-38.95, -103.79) * mm});
            skLineSegment(sketch, "E14.2.72", {"start": v(-32.83, -95.14) * mm, "end": v(-35.34, -92.12) * mm});
            skLineSegment(sketch, "E14.2.73", {"start": v(-44.97, -96.56) * mm, "end": v(-35.34, -92.12) * mm});
            skLineSegment(sketch, "E14.2.74", {"start": v(-44.18, -84.37) * mm, "end": v(-47.33, -94.49) * mm});
            skLineSegment(sketch, "E14.2.75", {"start": v(-44.18, -84.37) * mm, "end": v(-47.5, -82.27) * mm});
            skLineSegment(sketch, "E14.2.76", {"start": v(-55.28, -89.47) * mm, "end": v(-47.5, -82.27) * mm});
            skLineSegment(sketch, "E14.2.77", {"start": v(-58.3, -77.63) * mm, "end": v(-58.17, -88.23) * mm});
            skLineSegment(sketch, "E14.2.78", {"start": v(-58.3, -77.63) * mm, "end": v(-62.1, -76.67) * mm});
            skLineSegment(sketch, "E14.2.79", {"start": v(-67.28, -85.92) * mm, "end": v(-62.1, -76.67) * mm});
            skLineSegment(sketch, "E14.2.80", {"start": v(-73.8, -75.6) * mm, "end": v(-70.4, -85.63) * mm});
            skLineSegment(sketch, "E14.2.81", {"start": v(-73.8, -75.6) * mm, "end": v(-77.73, -75.85) * mm});
            skCircle(sketch, "E15", {"center": v(0, 0) * mm, "radius": 145 * mm});
            skPoint(sketch, "E16.middle", {"position": v(-35, 0) * mm});
            skLineSegment(sketch, "E17", {"start": v(0, 0) * mm, "end": v(70, 0) * mm});
            skArc(sketch, "E18", {"start": v(-10, -10) * mm, "mid": v(0, 0) * mm, "end": v(-10, 10) * mm});
            skArc(sketch, "E19", {"start": v(-60, 10) * mm, "mid": v(-70, 0) * mm, "end": v(-60, -10) * mm});
            skLineSegment(sketch, "E20", {"start": v(-60, 10) * mm, "end": v(-10, 10) * mm});
            skLineSegment(sketch, "E21", {"start": v(-10, -10) * mm, "end": v(-60, -10) * mm});
            skCircle(sketch, "E22", {"center": v(-35, 0) * mm, "radius": 10 * mm});
            skCircle(sketch, "E23", {"center": v(0, 0) * mm, "radius": 70 * mm});
            skCircle(sketch, "E24", {"center": v(0, 0) * mm, "radius": 90 * mm});
            skSolve(sketch);
        }
        {
            var Q0;
            {var subQ0=sQuery(id+"F0.wireOp",EDGE,"E2");Q0=makeQuery(id+"F0.imprint","IMPRINT",FACE,{"disambiguationData":[TD([[makeQuery(id+"F0.imprint","IMPRINT",EDGE,{"derivedFrom":subQ0}),-1.0]])]});}
            var Q1;
            {var subQ6=sQuery(id+"F0.wireOp",EDGE,"E17");Q1=makeQuery(id+"F0.imprint","IMPRINT",FACE,{"disambiguationData":[TD([[makeQuery(id+"F0.imprint","IMPRINT",EDGE,{"derivedFrom":subQ6}),1.0]])]});}
            var Q2;
            {var subQ8=sQuery(id+"F0.wireOp",EDGE,"E17");Q2=makeQuery(id+"F0.imprint","IMPRINT",FACE,{"disambiguationData":[TD([[makeQuery(id+"F0.imprint","IMPRINT",EDGE,{"derivedFrom":subQ8}),-1.0]])]});}
            var Q3;
            {var subQ0=sQuery(id+"F0.wireOp",EDGE,"E6.12.0");Q3=makeQuery(id+"F0.imprint","IMPRINT",FACE,{"disambiguationData":[TD([[makeQuery(id+"F0.imprint","IMPRINT",EDGE,{"derivedFrom":subQ0}),-1.0]])]});}
            var Q4;
            {var subQ0=sQuery(id+"F0.wireOp",EDGE,"E6.13.0");Q4=makeQuery(id+"F0.imprint","IMPRINT",FACE,{"disambiguationData":[TD([[makeQuery(id+"F0.imprint","IMPRINT",EDGE,{"derivedFrom":subQ0}),-1.0]])]});}
            var Q5;
            {var subQ0=sQuery(id+"F0.wireOp",EDGE,"E6.14.0");Q5=makeQuery(id+"F0.imprint","IMPRINT",FACE,{"disambiguationData":[TD([[makeQuery(id+"F0.imprint","IMPRINT",EDGE,{"derivedFrom":subQ0}),-1.0]])]});}
            var Q6;
            {var subQ0=sQuery(id+"F0.wireOp",EDGE,"E6.15.0");Q6=makeQuery(id+"F0.imprint","IMPRINT",FACE,{"disambiguationData":[TD([[makeQuery(id+"F0.imprint","IMPRINT",EDGE,{"derivedFrom":subQ0}),-1.0]])]});}
            var Q7;
            {var subQ0=sQuery(id+"F0.wireOp",EDGE,"E6.16.0");Q7=makeQuery(id+"F0.imprint","IMPRINT",FACE,{"disambiguationData":[TD([[makeQuery(id+"F0.imprint","IMPRINT",EDGE,{"derivedFrom":subQ0}),-1.0]])]});}
            var Q8;
            {var subQ0=sQuery(id+"F0.wireOp",EDGE,"E6.19.0");Q8=makeQuery(id+"F0.imprint","IMPRINT",FACE,{"disambiguationData":[TD([[makeQuery(id+"F0.imprint","IMPRINT",EDGE,{"derivedFrom":subQ0}),-1.0]])]});}
            var Q9;
            {var subQ0=sQuery(id+"F0.wireOp",EDGE,"E6.17.0");Q9=makeQuery(id+"F0.imprint","IMPRINT",FACE,{"disambiguationData":[TD([[makeQuery(id+"F0.imprint","IMPRINT",EDGE,{"derivedFrom":subQ0}),-1.0]])]});}
            var Q10;
            {var subQ0=sQuery(id+"F0.wireOp",EDGE,"E6.18.0");Q10=makeQuery(id+"F0.imprint","IMPRINT",FACE,{"disambiguationData":[TD([[makeQuery(id+"F0.imprint","IMPRINT",EDGE,{"derivedFrom":subQ0}),-1.0]])]});}
            var Q11;
            {var subQ0=sQuery(id+"F0.wireOp",EDGE,"E6.21.0");Q11=makeQuery(id+"F0.imprint","IMPRINT",FACE,{"disambiguationData":[TD([[makeQuery(id+"F0.imprint","IMPRINT",EDGE,{"derivedFrom":subQ0}),-1.0]])]});}
            var Q12;
            {var subQ0=sQuery(id+"F0.wireOp",EDGE,"E6.22.0");Q12=makeQuery(id+"F0.imprint","IMPRINT",FACE,{"disambiguationData":[TD([[makeQuery(id+"F0.imprint","IMPRINT",EDGE,{"derivedFrom":subQ0}),-1.0]])]});}
            var Q13;
            {var subQ0=sQuery(id+"F0.wireOp",EDGE,"E6.20.0");Q13=makeQuery(id+"F0.imprint","IMPRINT",FACE,{"disambiguationData":[TD([[makeQuery(id+"F0.imprint","IMPRINT",EDGE,{"derivedFrom":subQ0}),-1.0]])]});}
            var Q14;
            {var subQ0=sQuery(id+"F0.wireOp",EDGE,"E6.21.3");Q14=makeQuery(id+"F0.imprint","IMPRINT",FACE,{"disambiguationData":[TD([[makeQuery(id+"F0.imprint","IMPRINT",EDGE,{"derivedFrom":subQ0}),1.0]])]});}
            var Q15;
            {var subQ0=sQuery(id+"F0.wireOp",EDGE,"E6.19.3");Q15=makeQuery(id+"F0.imprint","IMPRINT",FACE,{"disambiguationData":[TD([[makeQuery(id+"F0.imprint","IMPRINT",EDGE,{"derivedFrom":subQ0}),1.0]])]});}
            var Q16;
            {var subQ0=sQuery(id+"F0.wireOp",EDGE,"E6.17.3");Q16=makeQuery(id+"F0.imprint","IMPRINT",FACE,{"disambiguationData":[TD([[makeQuery(id+"F0.imprint","IMPRINT",EDGE,{"derivedFrom":subQ0}),1.0]])]});}
            var Q17;
            {var subQ0=sQuery(id+"F0.wireOp",EDGE,"E6.23.3");Q17=makeQuery(id+"F0.imprint","IMPRINT",FACE,{"disambiguationData":[TD([[makeQuery(id+"F0.imprint","IMPRINT",EDGE,{"derivedFrom":subQ0}),1.0]])]});}
            var Q18;
            {var subQ0=sQuery(id+"F0.wireOp",EDGE,"E6.18.3");Q18=makeQuery(id+"F0.imprint","IMPRINT",FACE,{"disambiguationData":[TD([[makeQuery(id+"F0.imprint","IMPRINT",EDGE,{"derivedFrom":subQ0}),1.0]])]});}
            var Q19;
            {var subQ0=sQuery(id+"F0.wireOp",EDGE,"E6.20.3");Q19=makeQuery(id+"F0.imprint","IMPRINT",FACE,{"disambiguationData":[TD([[makeQuery(id+"F0.imprint","IMPRINT",EDGE,{"derivedFrom":subQ0}),1.0]])]});}
            var Q20;
            {var subQ0=sQuery(id+"F0.wireOp",EDGE,"E6.22.3");Q20=makeQuery(id+"F0.imprint","IMPRINT",FACE,{"disambiguationData":[TD([[makeQuery(id+"F0.imprint","IMPRINT",EDGE,{"derivedFrom":subQ0}),1.0]])]});}
            var Q21;
            {var subQ0=sQuery(id+"F0.wireOp",EDGE,"E6.16.3");Q21=makeQuery(id+"F0.imprint","IMPRINT",FACE,{"disambiguationData":[TD([[makeQuery(id+"F0.imprint","IMPRINT",EDGE,{"derivedFrom":subQ0}),1.0]])]});}
            var Q22;
            {var subQ0=sQuery(id+"F0.wireOp",EDGE,"E6.31.0");Q22=makeQuery(id+"F0.imprint","IMPRINT",FACE,{"disambiguationData":[TD([[makeQuery(id+"F0.imprint","IMPRINT",EDGE,{"derivedFrom":subQ0}),-1.0]])]});}
            var Q23;
            {var subQ0=sQuery(id+"F0.wireOp",EDGE,"E6.32.0");Q23=makeQuery(id+"F0.imprint","IMPRINT",FACE,{"disambiguationData":[TD([[makeQuery(id+"F0.imprint","IMPRINT",EDGE,{"derivedFrom":subQ0}),-1.0]])]});}
            var Q24;
            {var subQ0=sQuery(id+"F0.wireOp",EDGE,"E6.33.0");Q24=makeQuery(id+"F0.imprint","IMPRINT",FACE,{"disambiguationData":[TD([[makeQuery(id+"F0.imprint","IMPRINT",EDGE,{"derivedFrom":subQ0}),-1.0]])]});}
            var Q25;
            {var subQ0=sQuery(id+"F0.wireOp",EDGE,"E6.34.0");Q25=makeQuery(id+"F0.imprint","IMPRINT",FACE,{"disambiguationData":[TD([[makeQuery(id+"F0.imprint","IMPRINT",EDGE,{"derivedFrom":subQ0}),-1.0]])]});}
            var Q26;
            {var subQ0=sQuery(id+"F0.wireOp",EDGE,"E6.29.0");Q26=makeQuery(id+"F0.imprint","IMPRINT",FACE,{"disambiguationData":[TD([[makeQuery(id+"F0.imprint","IMPRINT",EDGE,{"derivedFrom":subQ0}),-1.0]])]});}
            var Q27;
            {var subQ0=sQuery(id+"F0.wireOp",EDGE,"E6.30.0");Q27=makeQuery(id+"F0.imprint","IMPRINT",FACE,{"disambiguationData":[TD([[makeQuery(id+"F0.imprint","IMPRINT",EDGE,{"derivedFrom":subQ0}),-1.0]])]});}
            var Q28;
            {var subQ25=sQuery(id+"F0.wireOp",EDGE,"E5");Q28=makeQuery(id+"F0.imprint","IMPRINT",FACE,{"disambiguationData":[TD([[makeQuery(id+"F0.imprint","IMPRINT",EDGE,{"derivedFrom":subQ25}),-1.0]])]});}
            var Q29;
            {var subQ0=sQuery(id+"F0.wireOp",EDGE,"E6.34.3");Q29=makeQuery(id+"F0.imprint","IMPRINT",FACE,{"disambiguationData":[TD([[makeQuery(id+"F0.imprint","IMPRINT",EDGE,{"derivedFrom":subQ0}),1.0]])]});}
            var Q30;
            {var subQ0=sQuery(id+"F0.wireOp",EDGE,"E6.35.3");Q30=makeQuery(id+"F0.imprint","IMPRINT",FACE,{"disambiguationData":[TD([[makeQuery(id+"F0.imprint","IMPRINT",EDGE,{"derivedFrom":subQ0}),1.0]])]});}
            var Q31;
            {var subQ0=sQuery(id+"F0.wireOp",EDGE,"E6.31.3");Q31=makeQuery(id+"F0.imprint","IMPRINT",FACE,{"disambiguationData":[TD([[makeQuery(id+"F0.imprint","IMPRINT",EDGE,{"derivedFrom":subQ0}),1.0]])]});}
            var Q32;
            {var subQ0=sQuery(id+"F0.wireOp",EDGE,"E6.33.3");Q32=makeQuery(id+"F0.imprint","IMPRINT",FACE,{"disambiguationData":[TD([[makeQuery(id+"F0.imprint","IMPRINT",EDGE,{"derivedFrom":subQ0}),1.0]])]});}
            var Q33;
            {var subQ0=sQuery(id+"F0.wireOp",EDGE,"E6.30.3");Q33=makeQuery(id+"F0.imprint","IMPRINT",FACE,{"disambiguationData":[TD([[makeQuery(id+"F0.imprint","IMPRINT",EDGE,{"derivedFrom":subQ0}),1.0]])]});}
            var Q34;
            {var subQ0=sQuery(id+"F0.wireOp",EDGE,"E6.29.3");Q34=makeQuery(id+"F0.imprint","IMPRINT",FACE,{"disambiguationData":[TD([[makeQuery(id+"F0.imprint","IMPRINT",EDGE,{"derivedFrom":subQ0}),1.0]])]});}
            var Q35;
            {var subQ0=sQuery(id+"F0.wireOp",EDGE,"E6.32.3");Q35=makeQuery(id+"F0.imprint","IMPRINT",FACE,{"disambiguationData":[TD([[makeQuery(id+"F0.imprint","IMPRINT",EDGE,{"derivedFrom":subQ0}),1.0]])]});}
            var Q36;
            {var subQ0=sQuery(id+"F0.wireOp",EDGE,"E6.28.0");Q36=makeQuery(id+"F0.imprint","IMPRINT",FACE,{"disambiguationData":[TD([[makeQuery(id+"F0.imprint","IMPRINT",EDGE,{"derivedFrom":subQ0}),-1.0]])]});}
            var Q37;
            {var subQ0=sQuery(id+"F0.wireOp",EDGE,"E6.27.0");Q37=makeQuery(id+"F0.imprint","IMPRINT",FACE,{"disambiguationData":[TD([[makeQuery(id+"F0.imprint","IMPRINT",EDGE,{"derivedFrom":subQ0}),-1.0]])]});}
            var Q38;
            {var subQ0=sQuery(id+"F0.wireOp",EDGE,"E6.26.0");Q38=makeQuery(id+"F0.imprint","IMPRINT",FACE,{"disambiguationData":[TD([[makeQuery(id+"F0.imprint","IMPRINT",EDGE,{"derivedFrom":subQ0}),-1.0]])]});}
            var Q39;
            {var subQ0=sQuery(id+"F0.wireOp",EDGE,"E6.25.0");Q39=makeQuery(id+"F0.imprint","IMPRINT",FACE,{"disambiguationData":[TD([[makeQuery(id+"F0.imprint","IMPRINT",EDGE,{"derivedFrom":subQ0}),-1.0]])]});}
            var Q40;
            {var subQ0=sQuery(id+"F0.wireOp",EDGE,"E6.24.0");Q40=makeQuery(id+"F0.imprint","IMPRINT",FACE,{"disambiguationData":[TD([[makeQuery(id+"F0.imprint","IMPRINT",EDGE,{"derivedFrom":subQ0}),-1.0]])]});}
            var Q41;
            {var subQ0=sQuery(id+"F0.wireOp",EDGE,"E6.23.0");Q41=makeQuery(id+"F0.imprint","IMPRINT",FACE,{"disambiguationData":[TD([[makeQuery(id+"F0.imprint","IMPRINT",EDGE,{"derivedFrom":subQ0}),-1.0]])]});}
            var Q42;
            {var subQ0=sQuery(id+"F0.wireOp",EDGE,"E6.35.0");Q42=makeQuery(id+"F0.imprint","IMPRINT",FACE,{"disambiguationData":[TD([[makeQuery(id+"F0.imprint","IMPRINT",EDGE,{"derivedFrom":subQ0}),-1.0]])]});}
            var Q43;
            {var subQ0=sQuery(id+"F0.wireOp",EDGE,"E6.1.0");Q43=makeQuery(id+"F0.imprint","IMPRINT",FACE,{"disambiguationData":[TD([[makeQuery(id+"F0.imprint","IMPRINT",EDGE,{"derivedFrom":subQ0}),-1.0]])]});}
            var Q44;
            {var subQ0=sQuery(id+"F0.wireOp",EDGE,"E6.2.0");Q44=makeQuery(id+"F0.imprint","IMPRINT",FACE,{"disambiguationData":[TD([[makeQuery(id+"F0.imprint","IMPRINT",EDGE,{"derivedFrom":subQ0}),-1.0]])]});}
            var Q45;
            {var subQ0=sQuery(id+"F0.wireOp",EDGE,"E6.3.0");Q45=makeQuery(id+"F0.imprint","IMPRINT",FACE,{"disambiguationData":[TD([[makeQuery(id+"F0.imprint","IMPRINT",EDGE,{"derivedFrom":subQ0}),-1.0]])]});}
            var Q46;
            {var subQ0=sQuery(id+"F0.wireOp",EDGE,"E6.4.0");Q46=makeQuery(id+"F0.imprint","IMPRINT",FACE,{"disambiguationData":[TD([[makeQuery(id+"F0.imprint","IMPRINT",EDGE,{"derivedFrom":subQ0}),-1.0]])]});}
            var Q47;
            {var subQ0=sQuery(id+"F0.wireOp",EDGE,"E6.5.0");Q47=makeQuery(id+"F0.imprint","IMPRINT",FACE,{"disambiguationData":[TD([[makeQuery(id+"F0.imprint","IMPRINT",EDGE,{"derivedFrom":subQ0}),-1.0]])]});}
            var Q48;
            {var subQ0=sQuery(id+"F0.wireOp",EDGE,"E6.6.0");Q48=makeQuery(id+"F0.imprint","IMPRINT",FACE,{"disambiguationData":[TD([[makeQuery(id+"F0.imprint","IMPRINT",EDGE,{"derivedFrom":subQ0}),-1.0]])]});}
            var Q49;
            {var subQ0=sQuery(id+"F0.wireOp",EDGE,"E6.7.0");Q49=makeQuery(id+"F0.imprint","IMPRINT",FACE,{"disambiguationData":[TD([[makeQuery(id+"F0.imprint","IMPRINT",EDGE,{"derivedFrom":subQ0}),-1.0]])]});}
            var Q50;
            {var subQ0=sQuery(id+"F0.wireOp",EDGE,"E6.11.0");Q50=makeQuery(id+"F0.imprint","IMPRINT",FACE,{"disambiguationData":[TD([[makeQuery(id+"F0.imprint","IMPRINT",EDGE,{"derivedFrom":subQ0}),-1.0]])]});}
            var Q51;
            {var subQ0=sQuery(id+"F0.wireOp",EDGE,"E6.10.0");Q51=makeQuery(id+"F0.imprint","IMPRINT",FACE,{"disambiguationData":[TD([[makeQuery(id+"F0.imprint","IMPRINT",EDGE,{"derivedFrom":subQ0}),-1.0]])]});}
            var Q52;
            {var subQ0=sQuery(id+"F0.wireOp",EDGE,"E6.9.0");Q52=makeQuery(id+"F0.imprint","IMPRINT",FACE,{"disambiguationData":[TD([[makeQuery(id+"F0.imprint","IMPRINT",EDGE,{"derivedFrom":subQ0}),-1.0]])]});}
            var Q53;
            {var subQ0=sQuery(id+"F0.wireOp",EDGE,"E6.8.0");Q53=makeQuery(id+"F0.imprint","IMPRINT",FACE,{"disambiguationData":[TD([[makeQuery(id+"F0.imprint","IMPRINT",EDGE,{"derivedFrom":subQ0}),-1.0]])]});}
            extrude(context, id + "F1", {"entities" : qUnion([Q0, Q1, Q2, Q3, Q4, Q5, Q6, Q7, Q8, Q9, Q10, Q11, Q12, Q13, Q14, Q15, Q16, Q17, Q18, Q19, Q20, Q21, Q22, Q23, Q24, Q25, Q26, Q27, Q28, Q29, Q30, Q31, Q32, Q33, Q34, Q35, Q36, Q37, Q38, Q39, Q40, Q41, Q42, Q43, Q44, Q45, Q46, Q47, Q48, Q49, Q50, Q51, Q52, Q53]), "depth" : 3 * mm, "offsetDistance" : 25 * mm});
        }
        {
            var Q0;
            {var subQ1=sQuery(id+"F0.wireOp",EDGE,"E13.5.0");Q0=makeQuery(id+"F0.imprint","IMPRINT",FACE,{"disambiguationData":[TD([[makeQuery(id+"F0.imprint","IMPRINT",EDGE,{"derivedFrom":subQ1}),1.0]])]});}
            var Q1;
            Q1=makeQuery(id+"F0.imprint","IMPRINT",FACE,{"disambiguationData":[TD([[makeQuery(id+"F0.imprint","IMPRINT",EDGE,{"derivedFrom":sQuery(id+"F0.wireOp",EDGE,"E9")}),-1.0]])]});
            var Q2;
            Q2=makeQuery(id+"F0.imprint","IMPRINT",FACE,{"disambiguationData":[TD([[makeQuery(id+"F0.imprint","IMPRINT",EDGE,{"derivedFrom":sQuery(id+"F0.wireOp",EDGE,"E13.1.0")}),1.0]])]});
            extrude(context, id + "F2", {"entities" : qUnion([Q0, Q1, Q2]), "depth" : 3 * mm, "offsetDistance" : 25 * mm});
        }
        {
            var Q0;
            Q0=makeQuery(id+"F0.imprint","IMPRINT",FACE,{"disambiguationData":[TD([[makeQuery(id+"F0.imprint","IMPRINT",EDGE,{"derivedFrom":sQuery(id+"F0.wireOp",EDGE,"E14.1.1")}),-1.0]])]});
            var Q1;
            Q1=makeQuery(id+"F0.imprint","IMPRINT",FACE,{"disambiguationData":[TD([[makeQuery(id+"F0.imprint","IMPRINT",EDGE,{"derivedFrom":sQuery(id+"F0.wireOp",EDGE,"E14.1.0")}),-1.0]])]});
            extrude(context, id + "F3", {"entities" : qUnion([Q0, Q1]), "depth" : 3 * mm, "offsetDistance" : 25 * mm});
        }
        {
            var Q0;
            Q0=makeQuery(id+"F0.imprint","IMPRINT",FACE,{"disambiguationData":[TD([[makeQuery(id+"F0.imprint","IMPRINT",EDGE,{"derivedFrom":sQuery(id+"F0.wireOp",EDGE,"E14.2.1")}),-1.0]])]});
            var Q1;
            Q1=makeQuery(id+"F0.imprint","IMPRINT",FACE,{"disambiguationData":[TD([[makeQuery(id+"F0.imprint","IMPRINT",EDGE,{"derivedFrom":sQuery(id+"F0.wireOp",EDGE,"E14.2.0")}),-1.0]])]});
            extrude(context, id + "F4", {"entities" : qUnion([Q0, Q1]), "depth" : 3 * mm, "offsetDistance" : 25 * mm});
        }
        {
            var Q0;
            {var subQ25=sQuery(id+"F0.wireOp",EDGE,"E5");Q0=makeQuery(id+"F0.imprint","IMPRINT",FACE,{"disambiguationData":[TD([[makeQuery(id+"F0.imprint","IMPRINT",EDGE,{"derivedFrom":subQ25}),-1.0]])]});}
            extrude(context, id + "F5", {"entities" : qUnion([Q0]), "depth" : 13.1 * mm, "offsetDistance" : 25 * mm, "hasSecondDirection" : true, "secondDirectionOppositeDirection" : true, "secondDirectionDepth" : -3.1 * mm});
        }
        {
            var Q0;
            Q0=makeQuery(id+"F5.opExtrude","SWEPT_BODY",BODY,{"disambiguationData":[OSD([sQuery(id+"F0.wireOp",EDGE,"E5"),sQuery(id+"F0.wireOp",EDGE,"E6.1.3"),sQuery(id+"F0.wireOp",EDGE,"E6.2.3"),sQuery(id+"F0.wireOp",EDGE,"E6.3.3"),sQuery(id+"F0.wireOp",EDGE,"E6.4.3"),sQuery(id+"F0.wireOp",EDGE,"E6.5.3"),sQuery(id+"F0.wireOp",EDGE,"E6.6.3"),sQuery(id+"F0.wireOp",EDGE,"E6.7.3"),sQuery(id+"F0.wireOp",EDGE,"E6.8.3"),sQuery(id+"F0.wireOp",EDGE,"E6.9.3"),sQuery(id+"F0.wireOp",EDGE,"E6.10.3"),sQuery(id+"F0.wireOp",EDGE,"E6.11.3"),sQuery(id+"F0.wireOp",EDGE,"E6.12.3"),sQuery(id+"F0.wireOp",EDGE,"E6.13.3"),sQuery(id+"F0.wireOp",EDGE,"E6.14.3"),sQuery(id+"F0.wireOp",EDGE,"E6.15.3"),sQuery(id+"F0.wireOp",EDGE,"E6.16.3"),sQuery(id+"F0.wireOp",EDGE,"E6.17.3"),sQuery(id+"F0.wireOp",EDGE,"E6.18.3"),sQuery(id+"F0.wireOp",EDGE,"E6.19.3"),sQuery(id+"F0.wireOp",EDGE,"E6.20.3"),sQuery(id+"F0.wireOp",EDGE,"E6.21.3"),sQuery(id+"F0.wireOp",EDGE,"E6.22.3"),sQuery(id+"F0.wireOp",EDGE,"E6.23.3"),sQuery(id+"F0.wireOp",EDGE,"E6.24.3"),sQuery(id+"F0.wireOp",EDGE,"E6.25.3"),sQuery(id+"F0.wireOp",EDGE,"E6.26.3"),sQuery(id+"F0.wireOp",EDGE,"E6.27.3"),sQuery(id+"F0.wireOp",EDGE,"E6.28.3"),sQuery(id+"F0.wireOp",EDGE,"E6.29.3"),sQuery(id+"F0.wireOp",EDGE,"E6.30.3"),sQuery(id+"F0.wireOp",EDGE,"E6.31.3"),sQuery(id+"F0.wireOp",EDGE,"E6.32.3"),sQuery(id+"F0.wireOp",EDGE,"E6.33.3"),sQuery(id+"F0.wireOp",EDGE,"E6.34.3"),sQuery(id+"F0.wireOp",EDGE,"E6.35.3"),sQuery(id+"F0.wireOp",EDGE,"E23"),sQuery(id+"F0.wireOp",EDGE,"E24")])]});
            transform(context, id + "F6", {"entities" : qUnion([Q0]), "transformType" : TransformType.TRANSLATION_3D, "dx" : 0 * mm, "dy" : 0 * mm, "dz" : -13.2 * mm, "makeCopy" : true});
        }
        {
            var Q0;
            Q0=makeQuery(id+"F6.opPattern","COPY",BODY,{"derivedFrom":makeQuery(id+"F5.opExtrude","SWEPT_BODY",BODY,{"disambiguationData":[OSD([sQuery(id+"F0.wireOp",EDGE,"E5"),sQuery(id+"F0.wireOp",EDGE,"E6.1.3"),sQuery(id+"F0.wireOp",EDGE,"E6.2.3"),sQuery(id+"F0.wireOp",EDGE,"E6.3.3"),sQuery(id+"F0.wireOp",EDGE,"E6.4.3"),sQuery(id+"F0.wireOp",EDGE,"E6.5.3"),sQuery(id+"F0.wireOp",EDGE,"E6.6.3"),sQuery(id+"F0.wireOp",EDGE,"E6.7.3"),sQuery(id+"F0.wireOp",EDGE,"E6.8.3"),sQuery(id+"F0.wireOp",EDGE,"E6.9.3"),sQuery(id+"F0.wireOp",EDGE,"E6.10.3"),sQuery(id+"F0.wireOp",EDGE,"E6.11.3"),sQuery(id+"F0.wireOp",EDGE,"E6.12.3"),sQuery(id+"F0.wireOp",EDGE,"E6.13.3"),sQuery(id+"F0.wireOp",EDGE,"E6.14.3"),sQuery(id+"F0.wireOp",EDGE,"E6.15.3"),sQuery(id+"F0.wireOp",EDGE,"E6.16.3"),sQuery(id+"F0.wireOp",EDGE,"E6.17.3"),sQuery(id+"F0.wireOp",EDGE,"E6.18.3"),sQuery(id+"F0.wireOp",EDGE,"E6.19.3"),sQuery(id+"F0.wireOp",EDGE,"E6.20.3"),sQuery(id+"F0.wireOp",EDGE,"E6.21.3"),sQuery(id+"F0.wireOp",EDGE,"E6.22.3"),sQuery(id+"F0.wireOp",EDGE,"E6.23.3"),sQuery(id+"F0.wireOp",EDGE,"E6.24.3"),sQuery(id+"F0.wireOp",EDGE,"E6.25.3"),sQuery(id+"F0.wireOp",EDGE,"E6.26.3"),sQuery(id+"F0.wireOp",EDGE,"E6.27.3"),sQuery(id+"F0.wireOp",EDGE,"E6.28.3"),sQuery(id+"F0.wireOp",EDGE,"E6.29.3"),sQuery(id+"F0.wireOp",EDGE,"E6.30.3"),sQuery(id+"F0.wireOp",EDGE,"E6.31.3"),sQuery(id+"F0.wireOp",EDGE,"E6.32.3"),sQuery(id+"F0.wireOp",EDGE,"E6.33.3"),sQuery(id+"F0.wireOp",EDGE,"E6.34.3"),sQuery(id+"F0.wireOp",EDGE,"E6.35.3"),sQuery(id+"F0.wireOp",EDGE,"E23"),sQuery(id+"F0.wireOp",EDGE,"E24")])]}),"instanceName":"1"});
            transform(context, id + "F7", {"entities" : qUnion([Q0]), "transformType" : TransformType.TRANSLATION_3D, "dx" : 0 * mm, "dy" : 0 * mm, "dz" : -99.9 * mm, "makeCopy" : true});
        }
        {
            var Q0;
            Q0=makeQuery(id+"F7.opPattern","COPY",FACE,{"derivedFrom":makeQuery(id+"F6.opPattern","COPY",FACE,{"derivedFrom":makeQuery(id+"F5.opExtrude","CAP_FACE",FACE,{"disambiguationData":[OSD([sQuery(id+"F0.wireOp",EDGE,"E5"),sQuery(id+"F0.wireOp",EDGE,"E6.1.3"),sQuery(id+"F0.wireOp",EDGE,"E6.2.3"),sQuery(id+"F0.wireOp",EDGE,"E6.3.3"),sQuery(id+"F0.wireOp",EDGE,"E6.4.3"),sQuery(id+"F0.wireOp",EDGE,"E6.5.3"),sQuery(id+"F0.wireOp",EDGE,"E6.6.3"),sQuery(id+"F0.wireOp",EDGE,"E6.7.3"),sQuery(id+"F0.wireOp",EDGE,"E6.8.3"),sQuery(id+"F0.wireOp",EDGE,"E6.9.3"),sQuery(id+"F0.wireOp",EDGE,"E6.10.3"),sQuery(id+"F0.wireOp",EDGE,"E6.11.3"),sQuery(id+"F0.wireOp",EDGE,"E6.12.3"),sQuery(id+"F0.wireOp",EDGE,"E6.13.3"),sQuery(id+"F0.wireOp",EDGE,"E6.14.3"),sQuery(id+"F0.wireOp",EDGE,"E6.15.3"),sQuery(id+"F0.wireOp",EDGE,"E6.16.3"),sQuery(id+"F0.wireOp",EDGE,"E6.17.3"),sQuery(id+"F0.wireOp",EDGE,"E6.18.3"),sQuery(id+"F0.wireOp",EDGE,"E6.19.3"),sQuery(id+"F0.wireOp",EDGE,"E6.20.3"),sQuery(id+"F0.wireOp",EDGE,"E6.21.3"),sQuery(id+"F0.wireOp",EDGE,"E6.22.3"),sQuery(id+"F0.wireOp",EDGE,"E6.23.3"),sQuery(id+"F0.wireOp",EDGE,"E6.24.3"),sQuery(id+"F0.wireOp",EDGE,"E6.25.3"),sQuery(id+"F0.wireOp",EDGE,"E6.26.3"),sQuery(id+"F0.wireOp",EDGE,"E6.27.3"),sQuery(id+"F0.wireOp",EDGE,"E6.28.3"),sQuery(id+"F0.wireOp",EDGE,"E6.29.3"),sQuery(id+"F0.wireOp",EDGE,"E6.30.3"),sQuery(id+"F0.wireOp",EDGE,"E6.31.3"),sQuery(id+"F0.wireOp",EDGE,"E6.32.3"),sQuery(id+"F0.wireOp",EDGE,"E6.33.3"),sQuery(id+"F0.wireOp",EDGE,"E6.34.3"),sQuery(id+"F0.wireOp",EDGE,"E6.35.3"),sQuery(id+"F0.wireOp",EDGE,"E23"),sQuery(id+"F0.wireOp",EDGE,"E24")])],"isStart":false}),"instanceName":"1"}),"instanceName":"1"});
            var sketch = newSketch(context, id + "F8", { "sketchPlane" : qUnion([Q0])});
            skCircle(sketch, "E25", {"center": v(0, 0) * mm, "radius": 90 * mm});
            skLineSegment(sketch, "E26", {"start": v(0, 0) * mm, "end": v(90, 0) * mm});
            skLineSegment(sketch, "E27", {"start": v(90, 0) * mm, "end": v(0, 0) * mm});
            skLineSegment(sketch, "E28", {"start": v(0, 0) * mm, "end": v(-90, 0) * mm});
            skLineSegment(sketch, "E29", {"start": v(0, 0) * mm, "end": v(0, -90) * mm});
            skLineSegment(sketch, "E30", {"start": v(0, 0) * mm, "end": v(0, 90) * mm});
            skCircle(sketch, "E31", {"center": v(0, 0) * mm, "radius": 10 * mm});
            skPoint(sketch, "E32", {"position": v(10, 0) * mm});
            skSolve(sketch);
        }
        {
            var Q0;
            Q0=makeQuery(id+"F7.opPattern","COPY",BODY,{"derivedFrom":makeQuery(id+"F6.opPattern","COPY",BODY,{"derivedFrom":makeQuery(id+"F5.opExtrude","SWEPT_BODY",BODY,{"disambiguationData":[OSD([sQuery(id+"F0.wireOp",EDGE,"E5"),sQuery(id+"F0.wireOp",EDGE,"E6.1.3"),sQuery(id+"F0.wireOp",EDGE,"E6.2.3"),sQuery(id+"F0.wireOp",EDGE,"E6.3.3"),sQuery(id+"F0.wireOp",EDGE,"E6.4.3"),sQuery(id+"F0.wireOp",EDGE,"E6.5.3"),sQuery(id+"F0.wireOp",EDGE,"E6.6.3"),sQuery(id+"F0.wireOp",EDGE,"E6.7.3"),sQuery(id+"F0.wireOp",EDGE,"E6.8.3"),sQuery(id+"F0.wireOp",EDGE,"E6.9.3"),sQuery(id+"F0.wireOp",EDGE,"E6.10.3"),sQuery(id+"F0.wireOp",EDGE,"E6.11.3"),sQuery(id+"F0.wireOp",EDGE,"E6.12.3"),sQuery(id+"F0.wireOp",EDGE,"E6.13.3"),sQuery(id+"F0.wireOp",EDGE,"E6.14.3"),sQuery(id+"F0.wireOp",EDGE,"E6.15.3"),sQuery(id+"F0.wireOp",EDGE,"E6.16.3"),sQuery(id+"F0.wireOp",EDGE,"E6.17.3"),sQuery(id+"F0.wireOp",EDGE,"E6.18.3"),sQuery(id+"F0.wireOp",EDGE,"E6.19.3"),sQuery(id+"F0.wireOp",EDGE,"E6.20.3"),sQuery(id+"F0.wireOp",EDGE,"E6.21.3"),sQuery(id+"F0.wireOp",EDGE,"E6.22.3"),sQuery(id+"F0.wireOp",EDGE,"E6.23.3"),sQuery(id+"F0.wireOp",EDGE,"E6.24.3"),sQuery(id+"F0.wireOp",EDGE,"E6.25.3"),sQuery(id+"F0.wireOp",EDGE,"E6.26.3"),sQuery(id+"F0.wireOp",EDGE,"E6.27.3"),sQuery(id+"F0.wireOp",EDGE,"E6.28.3"),sQuery(id+"F0.wireOp",EDGE,"E6.29.3"),sQuery(id+"F0.wireOp",EDGE,"E6.30.3"),sQuery(id+"F0.wireOp",EDGE,"E6.31.3"),sQuery(id+"F0.wireOp",EDGE,"E6.32.3"),sQuery(id+"F0.wireOp",EDGE,"E6.33.3"),sQuery(id+"F0.wireOp",EDGE,"E6.34.3"),sQuery(id+"F0.wireOp",EDGE,"E6.35.3"),sQuery(id+"F0.wireOp",EDGE,"E23"),sQuery(id+"F0.wireOp",EDGE,"E24")])]}),"instanceName":"1"}),"instanceName":"1"});
            deleteBodies(context, id + "F9", {"entities" : qUnion([Q0])});
        }
        {
            var Q0;
            Q0=qCreatedBy(makeId("Front.planeOp"),FACE);
            var sketch = newSketch(context, id + "F10", { "sketchPlane" : qUnion([Q0])});
            skSolve(sketch);
        }
        {
            var Q0;
            {var subQ1=sQuery(id+"F8.wireOp",EDGE,"E28");var subQ3=sQuery(id+"F8.wireOp",EDGE,"E31");var subQ4=makeQuery(id+"F8.imprint","INTERSECT",VERTEX,{"derivedFrom":[subQ1,subQ3]});Q0=makeQuery(id+"F8.imprint","IMPRINT",FACE,{"disambiguationData":[TD([[makeQuery(id+"F8.imprint","IMPRINT",EDGE,{"disambiguationData":[TD([[subQ4,-1.0]])],"derivedFrom":subQ3}),1.0]])]});}
            var Q1;
            {var subQ1=sQuery(id+"F8.wireOp",EDGE,"E28");var subQ3=sQuery(id+"F8.wireOp",EDGE,"E31");var subQ4=makeQuery(id+"F8.imprint","INTERSECT",VERTEX,{"derivedFrom":[subQ1,subQ3]});Q1=makeQuery(id+"F8.imprint","IMPRINT",FACE,{"disambiguationData":[TD([[makeQuery(id+"F8.imprint","IMPRINT",EDGE,{"disambiguationData":[TD([[subQ4,1.0]])],"derivedFrom":subQ3}),1.0]])]});}
            var Q2;
            {var subQ1=sQuery(id+"F8.wireOp",EDGE,"E27");var subQ3=sQuery(id+"F8.wireOp",EDGE,"E31");var subQ4=makeQuery(id+"F8.imprint","INTERSECT",VERTEX,{"derivedFrom":[subQ1,subQ3]});Q2=makeQuery(id+"F8.imprint","IMPRINT",FACE,{"disambiguationData":[TD([[makeQuery(id+"F8.imprint","IMPRINT",EDGE,{"disambiguationData":[TD([[subQ4,-1.0]])],"derivedFrom":subQ3}),1.0]])]});}
            var Q3;
            {var subQ1=sQuery(id+"F8.wireOp",EDGE,"E27");var subQ3=sQuery(id+"F8.wireOp",EDGE,"E31");var subQ4=makeQuery(id+"F8.imprint","INTERSECT",VERTEX,{"derivedFrom":[subQ1,subQ3]});Q3=makeQuery(id+"F8.imprint","IMPRINT",FACE,{"disambiguationData":[TD([[makeQuery(id+"F8.imprint","IMPRINT",EDGE,{"disambiguationData":[TD([[subQ4,1.0]])],"derivedFrom":subQ3}),1.0]])]});}
            var Q4;
            Q4 = qSketchRegion(id + "F10", true);
            extrude(context, id + "F11", {"entities" : qUnion([Q0, Q1, Q2, Q3, Q4]), "depth" : 20 * mm, "offsetDistance" : 25 * mm});
        }
        {
            var Q0;
            Q0=qCreatedBy(makeId("Front.planeOp"),FACE);
            var sketch = newSketch(context, id + "F12", { "sketchPlane" : qUnion([Q0])});
            skLineSegment(sketch, "E33", {"start": v(0, -80) * mm, "end": v(-35, 0) * mm});
            skLineSegment(sketch, "E34", {"start": v(-35, 0) * mm, "end": v(-70, 80) * mm});
            skLineSegment(sketch, "E35", {"start": v(0, -80) * mm, "end": v(9.16, -76) * mm});
            skLineSegment(sketch, "E36", {"start": v(0, -80) * mm, "end": v(-9.16, -84) * mm});
            skSolve(sketch);
        }
        {
            var Q0;
            Q0=qCreatedBy(makeId("Right.planeOp"),FACE);
            var sketch = newSketch(context, id + "F13", { "sketchPlane" : qUnion([Q0])});
            skLineSegment(sketch, "E37.top", {"start": v(0, -80) * mm, "end": v(-10, -80) * mm});
            skSolve(sketch);
        }
        {
            var Q0;
            Q0=sQuery(id+"F12.wireOp",VERTEX,"E35.end");
            var Q1;
            Q1=sQuery(id+"F13.wireOp",VERTEX,"E37.top.end");
            var Q2;
            Q2=sQuery(id+"F12.wireOp",VERTEX,"E36.end");
            cPlane(context, id + "F14", {"entities" : qUnion([Q0, Q1, Q2]), "cplaneType" : CPlaneType.THREE_POINT, "offset" : 25 * mm, "width" : 150 * mm, "height" : 150 * mm});
        }
        {
            var Q0;
            Q0=qCreatedBy(id+"F14.planeOp",FACE);
            var sketch = newSketch(context, id + "F15", { "sketchPlane" : qUnion([Q0])});
            skCircle(sketch, "E38", {"center": v(-32.1, 0) * mm, "radius": 10 * mm});
            skSolve(sketch);
        }
        {
            var Q0;
            Q0=makeQuery(id+"F15.imprint","IMPRINT",FACE,{"disambiguationData":[TD([[makeQuery(id+"F15.imprint","IMPRINT",EDGE,{"derivedFrom":sQuery(id+"F15.wireOp",EDGE,"E38")}),1.0]])]});
            var Q1;
            Q1=sQuery(id+"F12.wireOp",EDGE,"E33");
            var Q2;
            Q2=sQuery(id+"F12.wireOp",EDGE,"E34");
            sweep(context, id + "F16", {"profiles" : qUnion([Q0]), "path" : qUnion([Q1, Q2])});
        }
    });
